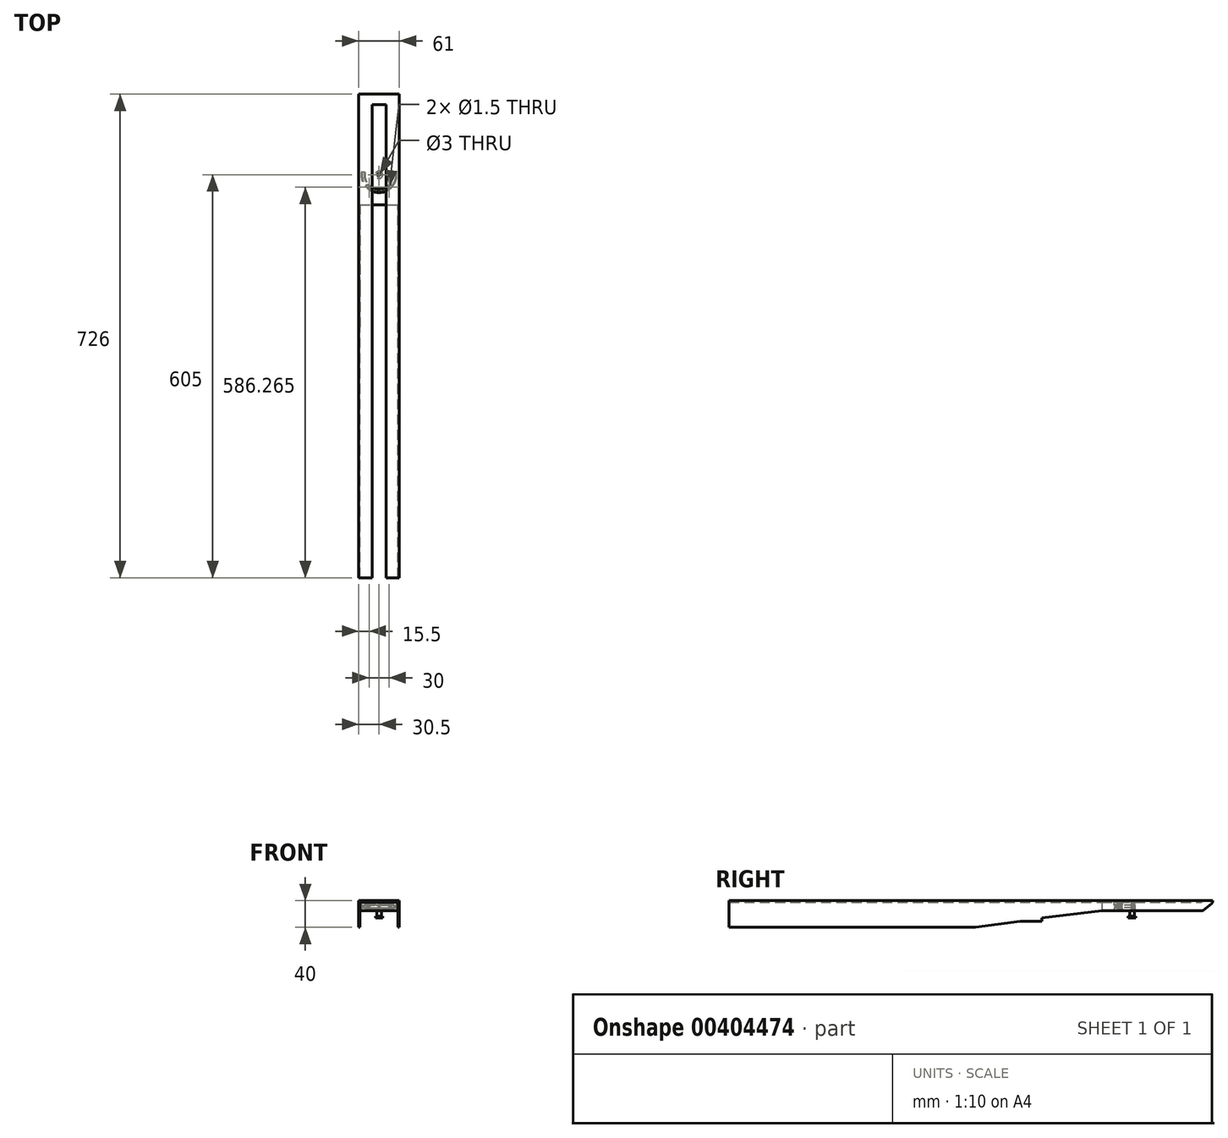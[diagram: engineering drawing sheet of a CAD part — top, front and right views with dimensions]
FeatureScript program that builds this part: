
annotation { "Feature Type Name" : "Feature", "Feature Type Description" : "" }
export const myFeature = defineFeature(function(context is Context, id is Id, definition is map)
    precondition{}
    {
        {
            var Q0;
            Q0=qCreatedBy(makeId("Top.planeOp"),FACE);
            var sketch = newSketch(context, id + "F0", { "sketchPlane" : qUnion([Q0])});
            skCircle(sketch, "E0", {"center": v(0, 0) * mm, "radius": 3.5 * mm});
            skLineSegment(sketch, "E1", {"start": v(-3.5, 0) * mm, "end": v(-3.5, -15.5) * mm});
            skLineSegment(sketch, "E2", {"start": v(3.5, 0) * mm, "end": v(3.5, -15.5) * mm});
            skLineSegment(sketch, "E3", {"start": v(-3.5, -15.5) * mm, "end": v(-7.78, -32.07) * mm});
            skLineSegment(sketch, "E4", {"start": v(3.5, -15.5) * mm, "end": v(7.78, -32.07) * mm});
            skLineSegment(sketch, "E5", {"start": v(-3.5, -15.5) * mm, "end": v(3.5, -15.5) * mm, "construction": true});
            skCircle(sketch, "E6", {"center": v(0, 0) * mm, "radius": 33 * mm});
            skLineSegment(sketch, "E7", {"start": v(-7.78, -32.07) * mm, "end": v(7.78, -32.07) * mm});
            skSolve(sketch);
        }
        {
            var Q0;
            Q0=qCreatedBy(makeId("Top.planeOp"),FACE);
            var sketch = newSketch(context, id + "F1", { "sketchPlane" : qUnion([Q0])});
            skLineSegment(sketch, "E8.bottom", {"start": v(-28.5, 105) * mm, "end": v(28.5, 105) * mm});
            skLineSegment(sketch, "E8.top", {"start": v(-28.5, -45) * mm, "end": v(28.5, -45) * mm});
            skLineSegment(sketch, "E8.left", {"start": v(-28.5, 105) * mm, "end": v(-28.5, -45) * mm});
            skLineSegment(sketch, "E8.right", {"start": v(28.5, 105) * mm, "end": v(28.5, -45) * mm});
            skPoint(sketch, "E8.middle", {"position": v(0, 0) * mm});
            skLineSegment(sketch, "E9", {"start": v(0, 105) * mm, "end": v(0, -45) * mm, "construction": true});
            skSolve(sketch);
        }
        {
            var Q0;
            Q0 = qSketchRegion(id + "F1", true);
            extrude(context, id + "F2", {"entities" : qUnion([Q0]), "depth" : 13 * mm});
        }
        {
            var Q0;
            Q0=qCreatedBy(makeId("Top.planeOp"),FACE);
            var sketch = newSketch(context, id + "F3", { "sketchPlane" : qUnion([Q0])});
            skLineSegment(sketch, "E10.bottom", {"start": v(-28.5, 33) * mm, "end": v(28.5, 33) * mm});
            skLineSegment(sketch, "E10.top", {"start": v(-28.5, -33) * mm, "end": v(28.5, -33) * mm});
            skLineSegment(sketch, "E10.left", {"start": v(-28.5, 33) * mm, "end": v(-28.5, -33) * mm});
            skLineSegment(sketch, "E10.right", {"start": v(28.5, 33) * mm, "end": v(28.5, -33) * mm});
            skPoint(sketch, "E10.middle", {"position": v(0, 0) * mm});
            skLineSegment(sketch, "E11.2", {"start": v(3.37, -15) * mm, "end": v(8.02, -33) * mm});
            skLineSegment(sketch, "E11.3", {"start": v(-3.37, -15) * mm, "end": v(-8.02, -33) * mm});
            skPoint(sketch, "E12.orphan", {"position": v(-3.5, 0) * mm});
            skPoint(sketch, "E13.orphan", {"position": v(3.5, 0) * mm});
            skLineSegment(sketch, "E14", {"start": v(-3.37, -15) * mm, "end": v(3.37, -15) * mm});
            skPoint(sketch, "E15.orphan", {"position": v(3.5, -15.5) * mm});
            skPoint(sketch, "E16.orphan", {"position": v(-3.5, -15.5) * mm});
            skPoint(sketch, "E17.orphan", {"position": v(-7.78, -32.07) * mm});
            skPoint(sketch, "E18.orphan", {"position": v(7.78, -32.07) * mm});
            skCircle(sketch, "E19", {"center": v(0, 0) * mm, "radius": 24 * mm, "construction": true});
            skCircle(sketch, "E20", {"center": v(0, 0) * mm, "radius": 26.5 * mm});
            skLineSegment(sketch, "E21", {"start": v(0, 0) * mm, "end": v(26.01, -21.83) * mm});
            skLineSegment(sketch, "E22", {"start": v(0, 0) * mm, "end": v(-26.01, -21.83) * mm});
            skCircle(sketch, "E23", {"center": v(0, 0) * mm, "radius": 21.5 * mm});
            skCircle(sketch, "E24", {"center": v(0, 0) * mm, "radius": 5.5 * mm});
            skLineSegment(sketch, "E25", {"start": v(0, 0) * mm, "end": v(-38.48, 6.79) * mm});
            skLineSegment(sketch, "E26", {"start": v(0, 0) * mm, "end": v(34.56, 6.1) * mm});
            skCircle(sketch, "E27", {"center": v(0, 0) * mm, "radius": 33.96 * mm, "construction": true});
            skCircle(sketch, "E28", {"center": v(0, 0) * mm, "radius": 40.5 * mm});
            skCircle(sketch, "E29", {"center": v(-17.7, -36.42) * mm, "radius": 1.98 * mm});
            skCircle(sketch, "E30", {"center": v(0, 0) * mm, "radius": 25.25 * mm});
            skCircle(sketch, "E31", {"center": v(0, 0) * mm, "radius": 22.75 * mm});
            skCircle(sketch, "E32", {"center": v(0, 0) * mm, "radius": 26.75 * mm});
            skCircle(sketch, "E33", {"center": v(0, 0) * mm, "radius": 21.25 * mm});
            skCircle(sketch, "E34", {"center": v(0, 0) * mm, "radius": 22.5 * mm});
            skCircle(sketch, "E35", {"center": v(0, 0) * mm, "radius": 25.5 * mm});
            skPoint(sketch, "E36", {"position": v(-15, -18.73) * mm});
            skPoint(sketch, "E37", {"position": v(15, -18.73) * mm});
            skSolve(sketch);
        }
        {
            var Q0;
            {var subQ0=sQuery(id+"F3.wireOp",EDGE,"E30");var subQ1=sQuery(id+"F3.wireOp",EDGE,"E11.2");var subQ2=makeQuery(id+"F3.imprint","INTERSECT",VERTEX,{"derivedFrom":[subQ1,subQ0]});Q0=makeQuery(id+"F3.imprint","IMPRINT",FACE,{"disambiguationData":[TD([[makeQuery(id+"F3.imprint","IMPRINT",EDGE,{"disambiguationData":[TD([[subQ2,-1.0]])],"derivedFrom":subQ1}),-1.0]])]});}
            var Q1;
            {var subQ0=sQuery(id+"F3.wireOp",EDGE,"E30");var subQ1=sQuery(id+"F3.wireOp",EDGE,"E11.3");var subQ2=makeQuery(id+"F3.imprint","INTERSECT",VERTEX,{"derivedFrom":[subQ1,subQ0]});Q1=makeQuery(id+"F3.imprint","IMPRINT",FACE,{"disambiguationData":[TD([[makeQuery(id+"F3.imprint","IMPRINT",EDGE,{"disambiguationData":[TD([[subQ2,-1.0]])],"derivedFrom":subQ1}),-1.0]])]});}
            var Q2;
            {var subQ0=sQuery(id+"F3.wireOp",EDGE,"E23");var subQ1=sQuery(id+"F3.wireOp",EDGE,"E11.3");var subQ2=makeQuery(id+"F3.imprint","INTERSECT",VERTEX,{"derivedFrom":[subQ1,subQ0]});Q2=makeQuery(id+"F3.imprint","IMPRINT",FACE,{"disambiguationData":[TD([[makeQuery(id+"F3.imprint","IMPRINT",EDGE,{"disambiguationData":[TD([[subQ2,-1.0]])],"derivedFrom":subQ1}),-1.0]])]});}
            var Q3;
            {var subQ0=sQuery(id+"F3.wireOp",EDGE,"E31");var subQ1=sQuery(id+"F3.wireOp",EDGE,"E11.3");var subQ2=makeQuery(id+"F3.imprint","INTERSECT",VERTEX,{"derivedFrom":[subQ1,subQ0]});Q3=makeQuery(id+"F3.imprint","IMPRINT",FACE,{"disambiguationData":[TD([[makeQuery(id+"F3.imprint","IMPRINT",EDGE,{"disambiguationData":[TD([[subQ2,-1.0]])],"derivedFrom":subQ1}),-1.0]])]});}
            var Q4;
            {var subQ0=sQuery(id+"F3.wireOp",EDGE,"E31");var subQ1=sQuery(id+"F3.wireOp",EDGE,"E11.2");var subQ2=makeQuery(id+"F3.imprint","INTERSECT",VERTEX,{"derivedFrom":[subQ1,subQ0]});Q4=makeQuery(id+"F3.imprint","IMPRINT",FACE,{"disambiguationData":[TD([[makeQuery(id+"F3.imprint","IMPRINT",EDGE,{"disambiguationData":[TD([[subQ2,-1.0]])],"derivedFrom":subQ1}),-1.0]])]});}
            var Q5;
            {var subQ0=sQuery(id+"F3.wireOp",EDGE,"E30");var subQ1=sQuery(id+"F3.wireOp",EDGE,"E11.2");var subQ2=makeQuery(id+"F3.imprint","INTERSECT",VERTEX,{"derivedFrom":[subQ1,subQ0]});Q5=makeQuery(id+"F3.imprint","IMPRINT",FACE,{"disambiguationData":[TD([[makeQuery(id+"F3.imprint","IMPRINT",EDGE,{"disambiguationData":[TD([[subQ2,-1.0]])],"derivedFrom":subQ1}),1.0]])]});}
            var Q6;
            {var subQ0=sQuery(id+"F3.wireOp",EDGE,"E31");var subQ1=sQuery(id+"F3.wireOp",EDGE,"E11.2");var subQ2=makeQuery(id+"F3.imprint","INTERSECT",VERTEX,{"derivedFrom":[subQ1,subQ0]});Q6=makeQuery(id+"F3.imprint","IMPRINT",FACE,{"disambiguationData":[TD([[makeQuery(id+"F3.imprint","IMPRINT",EDGE,{"disambiguationData":[TD([[subQ2,-1.0]])],"derivedFrom":subQ1}),1.0]])]});}
            var Q7;
            {var subQ0=sQuery(id+"F3.wireOp",EDGE,"E23");var subQ1=sQuery(id+"F3.wireOp",EDGE,"E11.2");var subQ2=makeQuery(id+"F3.imprint","INTERSECT",VERTEX,{"derivedFrom":[subQ1,subQ0]});Q7=makeQuery(id+"F3.imprint","IMPRINT",FACE,{"disambiguationData":[TD([[makeQuery(id+"F3.imprint","IMPRINT",EDGE,{"disambiguationData":[TD([[subQ2,-1.0]])],"derivedFrom":subQ1}),1.0]])]});}
            var Q8;
            {var subQ0=sQuery(id+"F3.wireOp",EDGE,"E23");var subQ1=sQuery(id+"F3.wireOp",EDGE,"E11.2");var subQ2=makeQuery(id+"F3.imprint","INTERSECT",VERTEX,{"derivedFrom":[subQ1,subQ0]});Q8=makeQuery(id+"F3.imprint","IMPRINT",FACE,{"disambiguationData":[TD([[makeQuery(id+"F3.imprint","IMPRINT",EDGE,{"disambiguationData":[TD([[subQ2,-1.0]])],"derivedFrom":subQ1}),-1.0]])]});}
            var Q9;
            {var subQ0=sQuery(id+"F3.wireOp",EDGE,"E23");var subQ1=sQuery(id+"F3.wireOp",EDGE,"E21");var subQ2=makeQuery(id+"F3.imprint","INTERSECT",VERTEX,{"derivedFrom":[subQ1,subQ0]});Q9=makeQuery(id+"F3.imprint","IMPRINT",FACE,{"disambiguationData":[TD([[makeQuery(id+"F3.imprint","IMPRINT",EDGE,{"disambiguationData":[TD([[subQ2,-1.0]])],"derivedFrom":subQ1}),1.0]])]});}
            var Q10;
            {var subQ0=sQuery(id+"F3.wireOp",EDGE,"E31");var subQ1=sQuery(id+"F3.wireOp",EDGE,"E21");var subQ2=makeQuery(id+"F3.imprint","INTERSECT",VERTEX,{"derivedFrom":[subQ1,subQ0]});Q10=makeQuery(id+"F3.imprint","IMPRINT",FACE,{"disambiguationData":[TD([[makeQuery(id+"F3.imprint","IMPRINT",EDGE,{"disambiguationData":[TD([[subQ2,-1.0]])],"derivedFrom":subQ1}),1.0]])]});}
            var Q11;
            {var subQ0=sQuery(id+"F3.wireOp",EDGE,"E21");var subQ1=sQuery(id+"F3.wireOp",EDGE,"E20");var subQ2=makeQuery(id+"F3.imprint","INTERSECT",VERTEX,{"derivedFrom":[subQ1,subQ0]});Q11=makeQuery(id+"F3.imprint","IMPRINT",FACE,{"disambiguationData":[TD([[makeQuery(id+"F3.imprint","IMPRINT",EDGE,{"disambiguationData":[TD([[subQ2,-1.0]])],"derivedFrom":subQ1}),1.0]])]});}
            var Q12;
            {var subQ0=sQuery(id+"F3.wireOp",EDGE,"E22");var subQ1=sQuery(id+"F3.wireOp",EDGE,"E20");var subQ2=makeQuery(id+"F3.imprint","INTERSECT",VERTEX,{"derivedFrom":[subQ1,subQ0]});Q12=makeQuery(id+"F3.imprint","IMPRINT",FACE,{"disambiguationData":[TD([[makeQuery(id+"F3.imprint","IMPRINT",EDGE,{"disambiguationData":[TD([[subQ2,1.0]])],"derivedFrom":subQ1}),1.0]])]});}
            var Q13;
            {var subQ0=sQuery(id+"F3.wireOp",EDGE,"E31");var subQ1=sQuery(id+"F3.wireOp",EDGE,"E22");var subQ2=makeQuery(id+"F3.imprint","INTERSECT",VERTEX,{"derivedFrom":[subQ1,subQ0]});Q13=makeQuery(id+"F3.imprint","IMPRINT",FACE,{"disambiguationData":[TD([[makeQuery(id+"F3.imprint","IMPRINT",EDGE,{"disambiguationData":[TD([[subQ2,-1.0]])],"derivedFrom":subQ1}),-1.0]])]});}
            var Q14;
            {var subQ0=sQuery(id+"F3.wireOp",EDGE,"E23");var subQ1=sQuery(id+"F3.wireOp",EDGE,"E22");var subQ2=makeQuery(id+"F3.imprint","INTERSECT",VERTEX,{"derivedFrom":[subQ1,subQ0]});Q14=makeQuery(id+"F3.imprint","IMPRINT",FACE,{"disambiguationData":[TD([[makeQuery(id+"F3.imprint","IMPRINT",EDGE,{"disambiguationData":[TD([[subQ2,-1.0]])],"derivedFrom":subQ1}),-1.0]])]});}
            var Q15;
            {var subQ0=sQuery(id+"F3.wireOp",EDGE,"E20");var subQ1=sQuery(id+"F3.wireOp",EDGE,"E11.2");var subQ2=makeQuery(id+"F3.imprint","INTERSECT",VERTEX,{"derivedFrom":[subQ1,subQ0]});Q15=makeQuery(id+"F3.imprint","IMPRINT",FACE,{"disambiguationData":[TD([[makeQuery(id+"F3.imprint","IMPRINT",EDGE,{"disambiguationData":[TD([[subQ2,-1.0]])],"derivedFrom":subQ1}),-1.0]])]});}
            var Q16;
            {var subQ0=sQuery(id+"F3.wireOp",EDGE,"E20");var subQ1=sQuery(id+"F3.wireOp",EDGE,"E11.3");var subQ2=makeQuery(id+"F3.imprint","INTERSECT",VERTEX,{"derivedFrom":[subQ1,subQ0]});Q16=makeQuery(id+"F3.imprint","IMPRINT",FACE,{"disambiguationData":[TD([[makeQuery(id+"F3.imprint","IMPRINT",EDGE,{"disambiguationData":[TD([[subQ2,-1.0]])],"derivedFrom":subQ1}),-1.0]])]});}
            var Q17;
            {var subQ0=sQuery(id+"F3.wireOp",EDGE,"E20");var subQ1=sQuery(id+"F3.wireOp",EDGE,"E11.2");var subQ2=makeQuery(id+"F3.imprint","INTERSECT",VERTEX,{"derivedFrom":[subQ1,subQ0]});Q17=makeQuery(id+"F3.imprint","IMPRINT",FACE,{"disambiguationData":[TD([[makeQuery(id+"F3.imprint","IMPRINT",EDGE,{"disambiguationData":[TD([[subQ2,-1.0]])],"derivedFrom":subQ1}),1.0]])]});}
            var Q18;
            {var subQ0=sQuery(id+"F3.wireOp",EDGE,"E33");var subQ1=sQuery(id+"F3.wireOp",EDGE,"E11.2");var subQ2=makeQuery(id+"F3.imprint","INTERSECT",VERTEX,{"derivedFrom":[subQ1,subQ0]});Q18=makeQuery(id+"F3.imprint","IMPRINT",FACE,{"disambiguationData":[TD([[makeQuery(id+"F3.imprint","IMPRINT",EDGE,{"disambiguationData":[TD([[subQ2,-1.0]])],"derivedFrom":subQ1}),1.0]])]});}
            var Q19;
            {var subQ0=sQuery(id+"F3.wireOp",EDGE,"E33");var subQ1=sQuery(id+"F3.wireOp",EDGE,"E11.2");var subQ2=makeQuery(id+"F3.imprint","INTERSECT",VERTEX,{"derivedFrom":[subQ1,subQ0]});Q19=makeQuery(id+"F3.imprint","IMPRINT",FACE,{"disambiguationData":[TD([[makeQuery(id+"F3.imprint","IMPRINT",EDGE,{"disambiguationData":[TD([[subQ2,-1.0]])],"derivedFrom":subQ1}),-1.0]])]});}
            var Q20;
            {var subQ0=sQuery(id+"F3.wireOp",EDGE,"E33");var subQ1=sQuery(id+"F3.wireOp",EDGE,"E11.3");var subQ2=makeQuery(id+"F3.imprint","INTERSECT",VERTEX,{"derivedFrom":[subQ1,subQ0]});Q20=makeQuery(id+"F3.imprint","IMPRINT",FACE,{"disambiguationData":[TD([[makeQuery(id+"F3.imprint","IMPRINT",EDGE,{"disambiguationData":[TD([[subQ2,-1.0]])],"derivedFrom":subQ1}),-1.0]])]});}
            var Q21;
            {var subQ0=sQuery(id+"F3.wireOp",EDGE,"E33");var subQ1=sQuery(id+"F3.wireOp",EDGE,"E22");var subQ2=makeQuery(id+"F3.imprint","INTERSECT",VERTEX,{"derivedFrom":[subQ1,subQ0]});Q21=makeQuery(id+"F3.imprint","IMPRINT",FACE,{"disambiguationData":[TD([[makeQuery(id+"F3.imprint","IMPRINT",EDGE,{"disambiguationData":[TD([[subQ2,-1.0]])],"derivedFrom":subQ1}),-1.0]])]});}
            var Q22;
            {var subQ0=sQuery(id+"F3.wireOp",EDGE,"E25");var subQ1=sQuery(id+"F3.wireOp",EDGE,"E20");var subQ2=makeQuery(id+"F3.imprint","INTERSECT",VERTEX,{"derivedFrom":[subQ1,subQ0]});Q22=makeQuery(id+"F3.imprint","IMPRINT",FACE,{"disambiguationData":[TD([[makeQuery(id+"F3.imprint","IMPRINT",EDGE,{"disambiguationData":[TD([[subQ2,-1.0]])],"derivedFrom":subQ1}),-1.0]])]});}
            var Q23;
            {var subQ0=sQuery(id+"F3.wireOp",EDGE,"E26");var subQ1=sQuery(id+"F3.wireOp",EDGE,"E20");var subQ2=makeQuery(id+"F3.imprint","INTERSECT",VERTEX,{"derivedFrom":[subQ1,subQ0]});Q23=makeQuery(id+"F3.imprint","IMPRINT",FACE,{"disambiguationData":[TD([[makeQuery(id+"F3.imprint","IMPRINT",EDGE,{"disambiguationData":[TD([[subQ2,1.0]])],"derivedFrom":subQ1}),-1.0]])]});}
            var Q24;
            {var subQ0=sQuery(id+"F3.wireOp",EDGE,"E33");var subQ1=sQuery(id+"F3.wireOp",EDGE,"E21");var subQ2=makeQuery(id+"F3.imprint","INTERSECT",VERTEX,{"derivedFrom":[subQ1,subQ0]});Q24=makeQuery(id+"F3.imprint","IMPRINT",FACE,{"disambiguationData":[TD([[makeQuery(id+"F3.imprint","IMPRINT",EDGE,{"disambiguationData":[TD([[subQ2,-1.0]])],"derivedFrom":subQ1}),1.0]])]});}
            var Q25;
            {var subQ0=sQuery(id+"F3.wireOp",EDGE,"E30");var subQ1=sQuery(id+"F3.wireOp",EDGE,"E22");var subQ2=makeQuery(id+"F3.imprint","INTERSECT",VERTEX,{"derivedFrom":[subQ1,subQ0]});Q25=makeQuery(id+"F3.imprint","IMPRINT",FACE,{"disambiguationData":[TD([[makeQuery(id+"F3.imprint","IMPRINT",EDGE,{"disambiguationData":[TD([[subQ2,-1.0]])],"derivedFrom":subQ1}),-1.0]])]});}
            var Q26;
            {var subQ0=sQuery(id+"F3.wireOp",EDGE,"E35");var subQ1=sQuery(id+"F3.wireOp",EDGE,"E11.3");var subQ2=makeQuery(id+"F3.imprint","INTERSECT",VERTEX,{"derivedFrom":[subQ1,subQ0]});Q26=makeQuery(id+"F3.imprint","IMPRINT",FACE,{"disambiguationData":[TD([[makeQuery(id+"F3.imprint","IMPRINT",EDGE,{"disambiguationData":[TD([[subQ2,-1.0]])],"derivedFrom":subQ1}),-1.0]])]});}
            var Q27;
            {var subQ0=sQuery(id+"F3.wireOp",EDGE,"E34");var subQ1=sQuery(id+"F3.wireOp",EDGE,"E11.3");var subQ2=makeQuery(id+"F3.imprint","INTERSECT",VERTEX,{"derivedFrom":[subQ1,subQ0]});Q27=makeQuery(id+"F3.imprint","IMPRINT",FACE,{"disambiguationData":[TD([[makeQuery(id+"F3.imprint","IMPRINT",EDGE,{"disambiguationData":[TD([[subQ2,-1.0]])],"derivedFrom":subQ1}),-1.0]])]});}
            var Q28;
            {var subQ0=sQuery(id+"F3.wireOp",EDGE,"E34");var subQ1=sQuery(id+"F3.wireOp",EDGE,"E22");var subQ2=makeQuery(id+"F3.imprint","INTERSECT",VERTEX,{"derivedFrom":[subQ1,subQ0]});Q28=makeQuery(id+"F3.imprint","IMPRINT",FACE,{"disambiguationData":[TD([[makeQuery(id+"F3.imprint","IMPRINT",EDGE,{"disambiguationData":[TD([[subQ2,-1.0]])],"derivedFrom":subQ1}),-1.0]])]});}
            var Q29;
            {var subQ0=sQuery(id+"F3.wireOp",EDGE,"E35");var subQ1=sQuery(id+"F3.wireOp",EDGE,"E11.2");var subQ2=makeQuery(id+"F3.imprint","INTERSECT",VERTEX,{"derivedFrom":[subQ1,subQ0]});Q29=makeQuery(id+"F3.imprint","IMPRINT",FACE,{"disambiguationData":[TD([[makeQuery(id+"F3.imprint","IMPRINT",EDGE,{"disambiguationData":[TD([[subQ2,-1.0]])],"derivedFrom":subQ1}),1.0]])]});}
            var Q30;
            {var subQ0=sQuery(id+"F3.wireOp",EDGE,"E34");var subQ1=sQuery(id+"F3.wireOp",EDGE,"E11.2");var subQ2=makeQuery(id+"F3.imprint","INTERSECT",VERTEX,{"derivedFrom":[subQ1,subQ0]});Q30=makeQuery(id+"F3.imprint","IMPRINT",FACE,{"disambiguationData":[TD([[makeQuery(id+"F3.imprint","IMPRINT",EDGE,{"disambiguationData":[TD([[subQ2,-1.0]])],"derivedFrom":subQ1}),1.0]])]});}
            var Q31;
            {var subQ0=sQuery(id+"F3.wireOp",EDGE,"E35");var subQ1=sQuery(id+"F3.wireOp",EDGE,"E11.2");var subQ2=makeQuery(id+"F3.imprint","INTERSECT",VERTEX,{"derivedFrom":[subQ1,subQ0]});Q31=makeQuery(id+"F3.imprint","IMPRINT",FACE,{"disambiguationData":[TD([[makeQuery(id+"F3.imprint","IMPRINT",EDGE,{"disambiguationData":[TD([[subQ2,-1.0]])],"derivedFrom":subQ1}),-1.0]])]});}
            var Q32;
            {var subQ0=sQuery(id+"F3.wireOp",EDGE,"E34");var subQ1=sQuery(id+"F3.wireOp",EDGE,"E11.2");var subQ2=makeQuery(id+"F3.imprint","INTERSECT",VERTEX,{"derivedFrom":[subQ1,subQ0]});Q32=makeQuery(id+"F3.imprint","IMPRINT",FACE,{"disambiguationData":[TD([[makeQuery(id+"F3.imprint","IMPRINT",EDGE,{"disambiguationData":[TD([[subQ2,-1.0]])],"derivedFrom":subQ1}),-1.0]])]});}
            var Q33;
            {var subQ0=sQuery(id+"F3.wireOp",EDGE,"E34");var subQ1=sQuery(id+"F3.wireOp",EDGE,"E21");var subQ2=makeQuery(id+"F3.imprint","INTERSECT",VERTEX,{"derivedFrom":[subQ1,subQ0]});Q33=makeQuery(id+"F3.imprint","IMPRINT",FACE,{"disambiguationData":[TD([[makeQuery(id+"F3.imprint","IMPRINT",EDGE,{"disambiguationData":[TD([[subQ2,-1.0]])],"derivedFrom":subQ1}),1.0]])]});}
            var Q34;
            {var subQ0=sQuery(id+"F3.wireOp",EDGE,"E30");var subQ1=sQuery(id+"F3.wireOp",EDGE,"E21");var subQ2=makeQuery(id+"F3.imprint","INTERSECT",VERTEX,{"derivedFrom":[subQ1,subQ0]});Q34=makeQuery(id+"F3.imprint","IMPRINT",FACE,{"disambiguationData":[TD([[makeQuery(id+"F3.imprint","IMPRINT",EDGE,{"disambiguationData":[TD([[subQ2,-1.0]])],"derivedFrom":subQ1}),1.0]])]});}
            extrude(context, id + "F4", {"entities" : qUnion([Q0, Q1, Q2, Q3, Q4, Q5, Q6, Q7, Q8, Q9, Q10, Q11, Q12, Q13, Q14, Q15, Q16, Q17, Q18, Q19, Q20, Q21, Q22, Q23, Q24, Q25, Q26, Q27, Q28, Q29, Q30, Q31, Q32, Q33, Q34]), "operationType" : NewBodyOperationType.REMOVE, "depth" : 4.5 * mm});
        }
        {
            var Q0;
            Q0=sQuery(id+"F0.wireOp",VERTEX,"E6.center");
            var Q1;
            Q1=makeQuery(id+"F2.opExtrude","SWEPT_BODY",BODY,{"disambiguationData":[OSD([sQuery(id+"F1.wireOp",EDGE,"E8.bottom"),sQuery(id+"F1.wireOp",EDGE,"E8.top"),sQuery(id+"F1.wireOp",EDGE,"E8.left"),sQuery(id+"F1.wireOp",EDGE,"E8.right")])]});
            hole(context, id + "F5", {"style" : HoleStyle.SIMPLE, "endStyle" : HoleEndStyle.THROUGH, "oppositeDirection" : true, "holeDiameter" : 3 * mm, "tappedDepth" : 12 * mm, "tapClearance" : 3, "locations" : qUnion([Q0]), "scope" : qUnion([Q1])});
        }
        {
            var Q0;
            Q0=makeQuery(id+"F2.opExtrude","CAP_FACE",FACE,{"disambiguationData":[OSD([sQuery(id+"F1.wireOp",EDGE,"E8.bottom"),sQuery(id+"F1.wireOp",EDGE,"E8.top"),sQuery(id+"F1.wireOp",EDGE,"E8.left"),sQuery(id+"F1.wireOp",EDGE,"E8.right")])],"isStart":false});
            var sketch = newSketch(context, id + "F6", { "sketchPlane" : qUnion([Q0])});
            skArc(sketch, "E38", {"start": v(20.93, 3.7) * mm, "mid": v(0, -21.25) * mm, "end": v(-20.93, 3.7) * mm});
            skArc(sketch, "E39", {"start": v(-26.34, 4.65) * mm, "mid": v(0, -26.75) * mm, "end": v(26.34, 4.65) * mm});
            skLineSegment(sketch, "E40", {"start": v(20.93, 3.7) * mm, "end": v(26.34, 4.65) * mm});
            skLineSegment(sketch, "E41", {"start": v(-26.34, 4.65) * mm, "end": v(-20.93, 3.7) * mm});
            skSolve(sketch);
        }
        {
            var Q0;
            Q0 = qSketchRegion(id + "F6", true);
            extrude(context, id + "F7", {"entities" : qUnion([Q0]), "operationType" : NewBodyOperationType.REMOVE, "oppositeDirection" : true, "depth" : 4.5 * mm});
        }
        {
            var Q0;
            {var subQ0=sQuery(id+"F3.wireOp",EDGE,"E31");var subQ1=sQuery(id+"F3.wireOp",EDGE,"E11.2");var subQ2=makeQuery(id+"F3.imprint","INTERSECT",VERTEX,{"derivedFrom":[subQ1,subQ0]});Q0=makeQuery(id+"F3.imprint","IMPRINT",FACE,{"disambiguationData":[TD([[makeQuery(id+"F3.imprint","IMPRINT",EDGE,{"disambiguationData":[TD([[subQ2,-1.0]])],"derivedFrom":subQ1}),-1.0]])]});}
            var Q1;
            {var subQ0=sQuery(id+"F3.wireOp",EDGE,"E30");var subQ1=sQuery(id+"F3.wireOp",EDGE,"E11.2");var subQ2=makeQuery(id+"F3.imprint","INTERSECT",VERTEX,{"derivedFrom":[subQ1,subQ0]});Q1=makeQuery(id+"F3.imprint","IMPRINT",FACE,{"disambiguationData":[TD([[makeQuery(id+"F3.imprint","IMPRINT",EDGE,{"disambiguationData":[TD([[subQ2,-1.0]])],"derivedFrom":subQ1}),-1.0]])]});}
            var Q2;
            {var subQ0=sQuery(id+"F3.wireOp",EDGE,"E34");var subQ1=sQuery(id+"F3.wireOp",EDGE,"E11.2");var subQ2=makeQuery(id+"F3.imprint","INTERSECT",VERTEX,{"derivedFrom":[subQ1,subQ0]});Q2=makeQuery(id+"F3.imprint","IMPRINT",FACE,{"disambiguationData":[TD([[makeQuery(id+"F3.imprint","IMPRINT",EDGE,{"disambiguationData":[TD([[subQ2,-1.0]])],"derivedFrom":subQ1}),-1.0]])]});}
            var Q3;
            {var subQ0=sQuery(id+"F3.wireOp",EDGE,"E34");var subQ1=sQuery(id+"F3.wireOp",EDGE,"E11.3");var subQ2=makeQuery(id+"F3.imprint","INTERSECT",VERTEX,{"derivedFrom":[subQ1,subQ0]});Q3=makeQuery(id+"F3.imprint","IMPRINT",FACE,{"disambiguationData":[TD([[makeQuery(id+"F3.imprint","IMPRINT",EDGE,{"disambiguationData":[TD([[subQ2,-1.0]])],"derivedFrom":subQ1}),-1.0]])]});}
            var Q4;
            {var subQ0=sQuery(id+"F3.wireOp",EDGE,"E31");var subQ1=sQuery(id+"F3.wireOp",EDGE,"E11.3");var subQ2=makeQuery(id+"F3.imprint","INTERSECT",VERTEX,{"derivedFrom":[subQ1,subQ0]});Q4=makeQuery(id+"F3.imprint","IMPRINT",FACE,{"disambiguationData":[TD([[makeQuery(id+"F3.imprint","IMPRINT",EDGE,{"disambiguationData":[TD([[subQ2,-1.0]])],"derivedFrom":subQ1}),-1.0]])]});}
            var Q5;
            {var subQ0=sQuery(id+"F3.wireOp",EDGE,"E30");var subQ1=sQuery(id+"F3.wireOp",EDGE,"E11.3");var subQ2=makeQuery(id+"F3.imprint","INTERSECT",VERTEX,{"derivedFrom":[subQ1,subQ0]});Q5=makeQuery(id+"F3.imprint","IMPRINT",FACE,{"disambiguationData":[TD([[makeQuery(id+"F3.imprint","IMPRINT",EDGE,{"disambiguationData":[TD([[subQ2,-1.0]])],"derivedFrom":subQ1}),-1.0]])]});}
            var Q6;
            {var subQ0=sQuery(id+"F3.wireOp",EDGE,"E30");var subQ1=sQuery(id+"F3.wireOp",EDGE,"E22");var subQ2=makeQuery(id+"F3.imprint","INTERSECT",VERTEX,{"derivedFrom":[subQ1,subQ0]});Q6=makeQuery(id+"F3.imprint","IMPRINT",FACE,{"disambiguationData":[TD([[makeQuery(id+"F3.imprint","IMPRINT",EDGE,{"disambiguationData":[TD([[subQ2,-1.0]])],"derivedFrom":subQ1}),-1.0]])]});}
            var Q7;
            {var subQ0=sQuery(id+"F3.wireOp",EDGE,"E31");var subQ1=sQuery(id+"F3.wireOp",EDGE,"E22");var subQ2=makeQuery(id+"F3.imprint","INTERSECT",VERTEX,{"derivedFrom":[subQ1,subQ0]});Q7=makeQuery(id+"F3.imprint","IMPRINT",FACE,{"disambiguationData":[TD([[makeQuery(id+"F3.imprint","IMPRINT",EDGE,{"disambiguationData":[TD([[subQ2,-1.0]])],"derivedFrom":subQ1}),-1.0]])]});}
            var Q8;
            {var subQ0=sQuery(id+"F3.wireOp",EDGE,"E34");var subQ1=sQuery(id+"F3.wireOp",EDGE,"E22");var subQ2=makeQuery(id+"F3.imprint","INTERSECT",VERTEX,{"derivedFrom":[subQ1,subQ0]});Q8=makeQuery(id+"F3.imprint","IMPRINT",FACE,{"disambiguationData":[TD([[makeQuery(id+"F3.imprint","IMPRINT",EDGE,{"disambiguationData":[TD([[subQ2,-1.0]])],"derivedFrom":subQ1}),-1.0]])]});}
            var Q9;
            {var subQ0=sQuery(id+"F3.wireOp",EDGE,"E31");var subQ1=sQuery(id+"F3.wireOp",EDGE,"E11.2");var subQ2=makeQuery(id+"F3.imprint","INTERSECT",VERTEX,{"derivedFrom":[subQ1,subQ0]});Q9=makeQuery(id+"F3.imprint","IMPRINT",FACE,{"disambiguationData":[TD([[makeQuery(id+"F3.imprint","IMPRINT",EDGE,{"disambiguationData":[TD([[subQ2,-1.0]])],"derivedFrom":subQ1}),1.0]])]});}
            var Q10;
            {var subQ0=sQuery(id+"F3.wireOp",EDGE,"E31");var subQ1=sQuery(id+"F3.wireOp",EDGE,"E21");var subQ2=makeQuery(id+"F3.imprint","INTERSECT",VERTEX,{"derivedFrom":[subQ1,subQ0]});Q10=makeQuery(id+"F3.imprint","IMPRINT",FACE,{"disambiguationData":[TD([[makeQuery(id+"F3.imprint","IMPRINT",EDGE,{"disambiguationData":[TD([[subQ2,-1.0]])],"derivedFrom":subQ1}),1.0]])]});}
            var Q11;
            {var subQ0=sQuery(id+"F3.wireOp",EDGE,"E34");var subQ1=sQuery(id+"F3.wireOp",EDGE,"E21");var subQ2=makeQuery(id+"F3.imprint","INTERSECT",VERTEX,{"derivedFrom":[subQ1,subQ0]});Q11=makeQuery(id+"F3.imprint","IMPRINT",FACE,{"disambiguationData":[TD([[makeQuery(id+"F3.imprint","IMPRINT",EDGE,{"disambiguationData":[TD([[subQ2,-1.0]])],"derivedFrom":subQ1}),1.0]])]});}
            var Q12;
            {var subQ0=sQuery(id+"F3.wireOp",EDGE,"E34");var subQ1=sQuery(id+"F3.wireOp",EDGE,"E11.2");var subQ2=makeQuery(id+"F3.imprint","INTERSECT",VERTEX,{"derivedFrom":[subQ1,subQ0]});Q12=makeQuery(id+"F3.imprint","IMPRINT",FACE,{"disambiguationData":[TD([[makeQuery(id+"F3.imprint","IMPRINT",EDGE,{"disambiguationData":[TD([[subQ2,-1.0]])],"derivedFrom":subQ1}),1.0]])]});}
            var Q13;
            {var subQ0=sQuery(id+"F3.wireOp",EDGE,"E30");var subQ1=sQuery(id+"F3.wireOp",EDGE,"E11.2");var subQ2=makeQuery(id+"F3.imprint","INTERSECT",VERTEX,{"derivedFrom":[subQ1,subQ0]});Q13=makeQuery(id+"F3.imprint","IMPRINT",FACE,{"disambiguationData":[TD([[makeQuery(id+"F3.imprint","IMPRINT",EDGE,{"disambiguationData":[TD([[subQ2,-1.0]])],"derivedFrom":subQ1}),1.0]])]});}
            var Q14;
            {var subQ0=sQuery(id+"F3.wireOp",EDGE,"E30");var subQ1=sQuery(id+"F3.wireOp",EDGE,"E21");var subQ2=makeQuery(id+"F3.imprint","INTERSECT",VERTEX,{"derivedFrom":[subQ1,subQ0]});Q14=makeQuery(id+"F3.imprint","IMPRINT",FACE,{"disambiguationData":[TD([[makeQuery(id+"F3.imprint","IMPRINT",EDGE,{"disambiguationData":[TD([[subQ2,-1.0]])],"derivedFrom":subQ1}),1.0]])]});}
            extrude(context, id + "F8", {"entities" : qUnion([Q0, Q1, Q2, Q3, Q4, Q5, Q6, Q7, Q8, Q9, Q10, Q11, Q12, Q13, Q14]), "operationType" : NewBodyOperationType.REMOVE, "depth" : 25 * mm});
        }
        {
            var Q0;
            {var subQ0=sQuery(id+"F3.wireOp",EDGE,"E23");var subQ1=sQuery(id+"F3.wireOp",EDGE,"E11.2");var subQ2=makeQuery(id+"F3.imprint","INTERSECT",VERTEX,{"derivedFrom":[subQ1,subQ0]});Q0=makeQuery(id+"F3.imprint","IMPRINT",FACE,{"disambiguationData":[TD([[makeQuery(id+"F3.imprint","IMPRINT",EDGE,{"disambiguationData":[TD([[subQ2,-1.0]])],"derivedFrom":subQ1}),1.0]])]});}
            var Q1;
            {var subQ0=sQuery(id+"F3.wireOp",EDGE,"E23");var subQ1=sQuery(id+"F3.wireOp",EDGE,"E11.2");var subQ2=makeQuery(id+"F3.imprint","INTERSECT",VERTEX,{"derivedFrom":[subQ1,subQ0]});Q1=makeQuery(id+"F3.imprint","IMPRINT",FACE,{"disambiguationData":[TD([[makeQuery(id+"F3.imprint","IMPRINT",EDGE,{"disambiguationData":[TD([[subQ2,-1.0]])],"derivedFrom":subQ1}),-1.0]])]});}
            var Q2;
            {var subQ0=sQuery(id+"F3.wireOp",EDGE,"E23");var subQ1=sQuery(id+"F3.wireOp",EDGE,"E11.3");var subQ2=makeQuery(id+"F3.imprint","INTERSECT",VERTEX,{"derivedFrom":[subQ1,subQ0]});Q2=makeQuery(id+"F3.imprint","IMPRINT",FACE,{"disambiguationData":[TD([[makeQuery(id+"F3.imprint","IMPRINT",EDGE,{"disambiguationData":[TD([[subQ2,-1.0]])],"derivedFrom":subQ1}),-1.0]])]});}
            var Q3;
            {var subQ0=sQuery(id+"F3.wireOp",EDGE,"E31");var subQ1=sQuery(id+"F3.wireOp",EDGE,"E11.3");var subQ2=makeQuery(id+"F3.imprint","INTERSECT",VERTEX,{"derivedFrom":[subQ1,subQ0]});Q3=makeQuery(id+"F3.imprint","IMPRINT",FACE,{"disambiguationData":[TD([[makeQuery(id+"F3.imprint","IMPRINT",EDGE,{"disambiguationData":[TD([[subQ2,-1.0]])],"derivedFrom":subQ1}),-1.0]])]});}
            var Q4;
            {var subQ0=sQuery(id+"F3.wireOp",EDGE,"E30");var subQ1=sQuery(id+"F3.wireOp",EDGE,"E11.3");var subQ2=makeQuery(id+"F3.imprint","INTERSECT",VERTEX,{"derivedFrom":[subQ1,subQ0]});Q4=makeQuery(id+"F3.imprint","IMPRINT",FACE,{"disambiguationData":[TD([[makeQuery(id+"F3.imprint","IMPRINT",EDGE,{"disambiguationData":[TD([[subQ2,-1.0]])],"derivedFrom":subQ1}),-1.0]])]});}
            var Q5;
            {var subQ0=sQuery(id+"F3.wireOp",EDGE,"E30");var subQ1=sQuery(id+"F3.wireOp",EDGE,"E11.2");var subQ2=makeQuery(id+"F3.imprint","INTERSECT",VERTEX,{"derivedFrom":[subQ1,subQ0]});Q5=makeQuery(id+"F3.imprint","IMPRINT",FACE,{"disambiguationData":[TD([[makeQuery(id+"F3.imprint","IMPRINT",EDGE,{"disambiguationData":[TD([[subQ2,-1.0]])],"derivedFrom":subQ1}),-1.0]])]});}
            var Q6;
            {var subQ0=sQuery(id+"F3.wireOp",EDGE,"E31");var subQ1=sQuery(id+"F3.wireOp",EDGE,"E11.2");var subQ2=makeQuery(id+"F3.imprint","INTERSECT",VERTEX,{"derivedFrom":[subQ1,subQ0]});Q6=makeQuery(id+"F3.imprint","IMPRINT",FACE,{"disambiguationData":[TD([[makeQuery(id+"F3.imprint","IMPRINT",EDGE,{"disambiguationData":[TD([[subQ2,-1.0]])],"derivedFrom":subQ1}),-1.0]])]});}
            var Q7;
            {var subQ0=sQuery(id+"F3.wireOp",EDGE,"E30");var subQ1=sQuery(id+"F3.wireOp",EDGE,"E11.2");var subQ2=makeQuery(id+"F3.imprint","INTERSECT",VERTEX,{"derivedFrom":[subQ1,subQ0]});Q7=makeQuery(id+"F3.imprint","IMPRINT",FACE,{"disambiguationData":[TD([[makeQuery(id+"F3.imprint","IMPRINT",EDGE,{"disambiguationData":[TD([[subQ2,-1.0]])],"derivedFrom":subQ1}),1.0]])]});}
            var Q8;
            {var subQ0=sQuery(id+"F3.wireOp",EDGE,"E31");var subQ1=sQuery(id+"F3.wireOp",EDGE,"E11.2");var subQ2=makeQuery(id+"F3.imprint","INTERSECT",VERTEX,{"derivedFrom":[subQ1,subQ0]});Q8=makeQuery(id+"F3.imprint","IMPRINT",FACE,{"disambiguationData":[TD([[makeQuery(id+"F3.imprint","IMPRINT",EDGE,{"disambiguationData":[TD([[subQ2,-1.0]])],"derivedFrom":subQ1}),1.0]])]});}
            var Q9;
            {var subQ0=sQuery(id+"F3.wireOp",EDGE,"E34");var subQ1=sQuery(id+"F3.wireOp",EDGE,"E11.2");var subQ2=makeQuery(id+"F3.imprint","INTERSECT",VERTEX,{"derivedFrom":[subQ1,subQ0]});Q9=makeQuery(id+"F3.imprint","IMPRINT",FACE,{"disambiguationData":[TD([[makeQuery(id+"F3.imprint","IMPRINT",EDGE,{"disambiguationData":[TD([[subQ2,-1.0]])],"derivedFrom":subQ1}),1.0]])]});}
            var Q10;
            {var subQ0=sQuery(id+"F3.wireOp",EDGE,"E35");var subQ1=sQuery(id+"F3.wireOp",EDGE,"E11.2");var subQ2=makeQuery(id+"F3.imprint","INTERSECT",VERTEX,{"derivedFrom":[subQ1,subQ0]});Q10=makeQuery(id+"F3.imprint","IMPRINT",FACE,{"disambiguationData":[TD([[makeQuery(id+"F3.imprint","IMPRINT",EDGE,{"disambiguationData":[TD([[subQ2,-1.0]])],"derivedFrom":subQ1}),1.0]])]});}
            var Q11;
            {var subQ0=sQuery(id+"F3.wireOp",EDGE,"E34");var subQ1=sQuery(id+"F3.wireOp",EDGE,"E11.2");var subQ2=makeQuery(id+"F3.imprint","INTERSECT",VERTEX,{"derivedFrom":[subQ1,subQ0]});Q11=makeQuery(id+"F3.imprint","IMPRINT",FACE,{"disambiguationData":[TD([[makeQuery(id+"F3.imprint","IMPRINT",EDGE,{"disambiguationData":[TD([[subQ2,-1.0]])],"derivedFrom":subQ1}),-1.0]])]});}
            var Q12;
            {var subQ0=sQuery(id+"F3.wireOp",EDGE,"E34");var subQ1=sQuery(id+"F3.wireOp",EDGE,"E11.3");var subQ2=makeQuery(id+"F3.imprint","INTERSECT",VERTEX,{"derivedFrom":[subQ1,subQ0]});Q12=makeQuery(id+"F3.imprint","IMPRINT",FACE,{"disambiguationData":[TD([[makeQuery(id+"F3.imprint","IMPRINT",EDGE,{"disambiguationData":[TD([[subQ2,-1.0]])],"derivedFrom":subQ1}),-1.0]])]});}
            var Q13;
            {var subQ0=sQuery(id+"F3.wireOp",EDGE,"E35");var subQ1=sQuery(id+"F3.wireOp",EDGE,"E11.3");var subQ2=makeQuery(id+"F3.imprint","INTERSECT",VERTEX,{"derivedFrom":[subQ1,subQ0]});Q13=makeQuery(id+"F3.imprint","IMPRINT",FACE,{"disambiguationData":[TD([[makeQuery(id+"F3.imprint","IMPRINT",EDGE,{"disambiguationData":[TD([[subQ2,-1.0]])],"derivedFrom":subQ1}),-1.0]])]});}
            var Q14;
            {var subQ0=sQuery(id+"F3.wireOp",EDGE,"E35");var subQ1=sQuery(id+"F3.wireOp",EDGE,"E11.2");var subQ2=makeQuery(id+"F3.imprint","INTERSECT",VERTEX,{"derivedFrom":[subQ1,subQ0]});Q14=makeQuery(id+"F3.imprint","IMPRINT",FACE,{"disambiguationData":[TD([[makeQuery(id+"F3.imprint","IMPRINT",EDGE,{"disambiguationData":[TD([[subQ2,-1.0]])],"derivedFrom":subQ1}),-1.0]])]});}
            extrude(context, id + "F9", {"entities" : qUnion([Q0, Q1, Q2, Q3, Q4, Q5, Q6, Q7, Q8, Q9, Q10, Q11, Q12, Q13, Q14]), "depth" : 4 * mm});
        }
        {
            var Q0;
            {var subQ0=sQuery(id+"F3.wireOp",EDGE,"E14");Q0=makeQuery(id+"F3.imprint","IMPRINT",FACE,{"disambiguationData":[TD([[makeQuery(id+"F3.imprint","IMPRINT",EDGE,{"derivedFrom":subQ0}),-1.0]])]});}
            var Q1;
            {var subQ0=sQuery(id+"F3.wireOp",EDGE,"E23");var subQ1=sQuery(id+"F3.wireOp",EDGE,"E11.2");var subQ2=makeQuery(id+"F3.imprint","INTERSECT",VERTEX,{"derivedFrom":[subQ1,subQ0]});Q1=makeQuery(id+"F3.imprint","IMPRINT",FACE,{"disambiguationData":[TD([[makeQuery(id+"F3.imprint","IMPRINT",EDGE,{"disambiguationData":[TD([[subQ2,-1.0]])],"derivedFrom":subQ1}),-1.0]])]});}
            var Q2;
            {var subQ0=sQuery(id+"F3.wireOp",EDGE,"E11.2");var subQ1=sQuery(id+"F3.wireOp",EDGE,"E10.top");var subQ2=makeQuery(id+"F3.imprint","INTERSECT",VERTEX,{"derivedFrom":[subQ1,subQ0]});Q2=makeQuery(id+"F3.imprint","IMPRINT",FACE,{"disambiguationData":[TD([[makeQuery(id+"F3.imprint","IMPRINT",EDGE,{"disambiguationData":[TD([[subQ2,1.0]])],"derivedFrom":subQ1}),1.0]])]});}
            var Q3;
            {var subQ0=sQuery(id+"F3.wireOp",EDGE,"E30");var subQ1=sQuery(id+"F3.wireOp",EDGE,"E11.2");var subQ2=makeQuery(id+"F3.imprint","INTERSECT",VERTEX,{"derivedFrom":[subQ1,subQ0]});Q3=makeQuery(id+"F3.imprint","IMPRINT",FACE,{"disambiguationData":[TD([[makeQuery(id+"F3.imprint","IMPRINT",EDGE,{"disambiguationData":[TD([[subQ2,-1.0]])],"derivedFrom":subQ1}),-1.0]])]});}
            var Q4;
            {var subQ0=sQuery(id+"F3.wireOp",EDGE,"E31");var subQ1=sQuery(id+"F3.wireOp",EDGE,"E11.2");var subQ2=makeQuery(id+"F3.imprint","INTERSECT",VERTEX,{"derivedFrom":[subQ1,subQ0]});Q4=makeQuery(id+"F3.imprint","IMPRINT",FACE,{"disambiguationData":[TD([[makeQuery(id+"F3.imprint","IMPRINT",EDGE,{"disambiguationData":[TD([[subQ2,-1.0]])],"derivedFrom":subQ1}),-1.0]])]});}
            var Q5;
            {var subQ0=sQuery(id+"F3.wireOp",EDGE,"E20");var subQ1=sQuery(id+"F3.wireOp",EDGE,"E11.2");var subQ2=makeQuery(id+"F3.imprint","INTERSECT",VERTEX,{"derivedFrom":[subQ1,subQ0]});Q5=makeQuery(id+"F3.imprint","IMPRINT",FACE,{"disambiguationData":[TD([[makeQuery(id+"F3.imprint","IMPRINT",EDGE,{"disambiguationData":[TD([[subQ2,-1.0]])],"derivedFrom":subQ1}),-1.0]])]});}
            var Q6;
            {var subQ0=sQuery(id+"F3.wireOp",EDGE,"E33");var subQ1=sQuery(id+"F3.wireOp",EDGE,"E11.2");var subQ2=makeQuery(id+"F3.imprint","INTERSECT",VERTEX,{"derivedFrom":[subQ1,subQ0]});Q6=makeQuery(id+"F3.imprint","IMPRINT",FACE,{"disambiguationData":[TD([[makeQuery(id+"F3.imprint","IMPRINT",EDGE,{"disambiguationData":[TD([[subQ2,-1.0]])],"derivedFrom":subQ1}),-1.0]])]});}
            var Q7;
            {var subQ0=sQuery(id+"F3.wireOp",EDGE,"E35");var subQ1=sQuery(id+"F3.wireOp",EDGE,"E11.2");var subQ2=makeQuery(id+"F3.imprint","INTERSECT",VERTEX,{"derivedFrom":[subQ1,subQ0]});Q7=makeQuery(id+"F3.imprint","IMPRINT",FACE,{"disambiguationData":[TD([[makeQuery(id+"F3.imprint","IMPRINT",EDGE,{"disambiguationData":[TD([[subQ2,-1.0]])],"derivedFrom":subQ1}),-1.0]])]});}
            var Q8;
            {var subQ0=sQuery(id+"F3.wireOp",EDGE,"E34");var subQ1=sQuery(id+"F3.wireOp",EDGE,"E11.2");var subQ2=makeQuery(id+"F3.imprint","INTERSECT",VERTEX,{"derivedFrom":[subQ1,subQ0]});Q8=makeQuery(id+"F3.imprint","IMPRINT",FACE,{"disambiguationData":[TD([[makeQuery(id+"F3.imprint","IMPRINT",EDGE,{"disambiguationData":[TD([[subQ2,-1.0]])],"derivedFrom":subQ1}),-1.0]])]});}
            extrude(context, id + "F10", {"entities" : qUnion([Q0, Q1, Q2, Q3, Q4, Q5, Q6, Q7, Q8]), "operationType" : NewBodyOperationType.ADD, "oppositeDirection" : true, "depth" : 7 * mm});
        }
        {
            var Q0;
            Q0=makeQuery(id+"F2.opExtrude","CAP_FACE",FACE,{"disambiguationData":[OSD([sQuery(id+"F1.wireOp",EDGE,"E8.bottom"),sQuery(id+"F1.wireOp",EDGE,"E8.top"),sQuery(id+"F1.wireOp",EDGE,"E8.left"),sQuery(id+"F1.wireOp",EDGE,"E8.right")])],"isStart":false});
            var sketch = newSketch(context, id + "F11", { "sketchPlane" : qUnion([Q0])});
            skArc(sketch, "E42", {"start": v(-16.47, -13.82) * mm, "mid": v(0, -21.5) * mm, "end": v(16.47, -13.82) * mm});
            skArc(sketch, "E43", {"start": v(-20.3, -17.03) * mm, "mid": v(0, -26.5) * mm, "end": v(20.3, -17.03) * mm});
            skLineSegment(sketch, "E44", {"start": v(-16.47, -13.82) * mm, "end": v(-20.3, -17.03) * mm});
            skLineSegment(sketch, "E45", {"start": v(16.47, -13.82) * mm, "end": v(20.3, -17.03) * mm});
            skSolve(sketch);
        }
        {
            var Q0;
            Q0 = qSketchRegion(id + "F11", true);
            extrude(context, id + "F12", {"entities" : qUnion([Q0]), "oppositeDirection" : true, "depth" : 4 * mm});
        }
        {
            var Q0;
            Q0=makeQuery(id+"F2.opExtrude","SWEPT_FACE",FACE,{"disambiguationData":[OSD([sQuery(id+"F1.wireOp",EDGE,"E8.bottom")])]});
            var sketch = newSketch(context, id + "F13", { "sketchPlane" : qUnion([Q0])});
            skLineSegment(sketch, "E46", {"start": v(-10.5, 15) * mm, "end": v(-30.5, 15) * mm});
            skLineSegment(sketch, "E47", {"start": v(-30.5, 15) * mm, "end": v(-30.5, -25) * mm});
            skLineSegment(sketch, "E48", {"start": v(10.5, 15) * mm, "end": v(30.5, 15) * mm});
            skLineSegment(sketch, "E49", {"start": v(30.5, 15) * mm, "end": v(30.5, -25) * mm});
            skLineSegment(sketch, "E50", {"start": v(-10.5, 15) * mm, "end": v(-10.5, 13) * mm});
            skLineSegment(sketch, "E51", {"start": v(-10.5, 13) * mm, "end": v(-28.5, 13) * mm});
            skLineSegment(sketch, "E52", {"start": v(-28.5, 13) * mm, "end": v(-28.5, -25) * mm});
            skLineSegment(sketch, "E53", {"start": v(-28.5, -25) * mm, "end": v(-30.5, -25) * mm});
            skLineSegment(sketch, "E54", {"start": v(10.5, 15) * mm, "end": v(10.5, 13) * mm});
            skLineSegment(sketch, "E55", {"start": v(10.5, 13) * mm, "end": v(28.5, 13) * mm});
            skLineSegment(sketch, "E56", {"start": v(28.5, 13) * mm, "end": v(28.5, -25) * mm});
            skLineSegment(sketch, "E57", {"start": v(28.5, -25) * mm, "end": v(30.5, -25) * mm});
            skSolve(sketch);
        }
        {
            var Q0;
            Q0=makeQuery(id+"F13.imprint","IMPRINT",FACE,{"disambiguationData":[TD([[makeQuery(id+"F13.imprint","IMPRINT",EDGE,{"derivedFrom":sQuery(id+"F13.wireOp",EDGE,"E46")}),1.0]])]});
            extrude(context, id + "F14", {"entities" : qUnion([Q0]), "oppositeDirection" : true, "depth" : 710 * mm, "offsetDistance" : 25 * mm});
        }
        {
            var Q0;
            Q0=makeQuery(id+"F13.imprint","IMPRINT",FACE,{"disambiguationData":[TD([[makeQuery(id+"F13.imprint","IMPRINT",EDGE,{"derivedFrom":sQuery(id+"F13.wireOp",EDGE,"E48")}),-1.0]])]});
            extrude(context, id + "F15", {"entities" : qUnion([Q0]), "oppositeDirection" : true, "depth" : 710 * mm, "offsetDistance" : 25 * mm});
        }
        {
            var Q0;
            Q0=qCreatedBy(makeId("Right.planeOp"),FACE);
            var sketch = newSketch(context, id + "F16", { "sketchPlane" : qUnion([Q0])});
            skLineSegment(sketch, "E58", {"start": v(105, 0) * mm, "end": v(-45, 0) * mm});
            skLineSegment(sketch, "E59", {"start": v(105, 0) * mm, "end": v(105, 15) * mm});
            skLineSegment(sketch, "E60", {"start": v(-45, 0) * mm, "end": v(-135, -11) * mm});
            skLineSegment(sketch, "E61", {"start": v(-135, -11) * mm, "end": v(-135, -16) * mm});
            skLineSegment(sketch, "E62", {"start": v(-135, -16) * mm, "end": v(-168, -16) * mm});
            skLineSegment(sketch, "E63", {"start": v(-168, -16) * mm, "end": v(-235, -25) * mm});
            skLineSegment(sketch, "E64", {"start": v(-235, -25) * mm, "end": v(105, -25) * mm});
            skLineSegment(sketch, "E65", {"start": v(105, -25) * mm, "end": v(105, 0) * mm});
            skSolve(sketch);
        }
        {
            var Q0;
            Q0 = qSketchRegion(id + "F16", true);
            extrude(context, id + "F17", {"entities" : qUnion([Q0]), "operationType" : NewBodyOperationType.REMOVE, "endBound" : BoundingType.SYMMETRIC, "oppositeDirection" : true, "depth" : 100 * mm});
        }
        {
            var Q0;
            Q0=makeQuery(id+"F2.opExtrude","SWEPT_FACE",FACE,{"disambiguationData":[OSD([sQuery(id+"F1.wireOp",EDGE,"E8.bottom")])]});
            var sketch = newSketch(context, id + "F18", { "sketchPlane" : qUnion([Q0])});
            skLineSegment(sketch, "E66.bottom", {"start": v(-30.5, 15) * mm, "end": v(30.5, 15) * mm});
            skLineSegment(sketch, "E66.top", {"start": v(-30.5, 0) * mm, "end": v(30.5, 0) * mm});
            skLineSegment(sketch, "E66.left", {"start": v(-30.5, 15) * mm, "end": v(-30.5, 0) * mm});
            skLineSegment(sketch, "E66.right", {"start": v(30.5, 15) * mm, "end": v(30.5, 0) * mm});
            skSolve(sketch);
        }
        {
            var Q0;
            Q0=qCreatedBy(makeId("Right.planeOp"),FACE);
            var sketch = newSketch(context, id + "F19", { "sketchPlane" : qUnion([Q0])});
            skLineSegment(sketch, "E67", {"start": v(0, 8.42) * mm, "end": v(0, -12.04) * mm, "construction": true});
            skLineSegment(sketch, "E68", {"start": v(0, 0) * mm, "end": v(-3.5, 0) * mm});
            skLineSegment(sketch, "E69", {"start": v(-3.5, 0) * mm, "end": v(-3.5, -8) * mm});
            skLineSegment(sketch, "E70", {"start": v(-3.5, -8) * mm, "end": v(-5.5, -8) * mm});
            skLineSegment(sketch, "E71", {"start": v(-5.5, -8) * mm, "end": v(-5.5, -11) * mm});
            skLineSegment(sketch, "E72", {"start": v(-5.5, -11) * mm, "end": v(0, -11) * mm});
            skLineSegment(sketch, "E73", {"start": v(0, 0) * mm, "end": v(0, -11) * mm});
            skSolve(sketch);
        }
        {
            var Q0;
            Q0 = qSketchRegion(id + "F18", true);
            extrude(context, id + "F20", {"entities" : qUnion([Q0]), "operationType" : NewBodyOperationType.ADD, "depth" : 16 * mm});
        }
        {
            var Q0;
            Q0=makeQuery(id+"F19.imprint","IMPRINT",FACE,{"disambiguationData":[TD([[makeQuery(id+"F19.imprint","IMPRINT",EDGE,{"derivedFrom":sQuery(id+"F19.wireOp",EDGE,"E68")}),1.0]])]});
            var Q1;
            Q1=sQuery(id+"F19.wireOp",EDGE,"E73");
            revolve(context, id + "F21", {"entities" : qUnion([Q0]), "axis" : qUnion([Q1]), "revolveType" : RevolveType.FULL});
        }
        {
            var Q0;
            Q0=makeQuery(id+"F20.opExtrude","CAP_EDGE",EDGE,{"disambiguationData":[OSD([sQuery(id+"F18.wireOp",EDGE,"E66.top")])],"isStart":false});
            chamfer(context, id + "F22", {"entities" : qUnion([Q0]), "chamferType" : ChamferType.OFFSET_ANGLE, "width" : 12 * mm, "oppositeDirection" : false, "angle" : 50 * degree, "tangentPropagation" : true});
        }
        {
            var Q0;
            {var subQ0=sQuery(id+"F18.wireOp",EDGE,"E66.top");Q0=makeQuery(id+"F22.opChamfer","BLEND_EDGE",EDGE,{"blendedFrom":[makeQuery(id+"F20.opExtrude","CAP_EDGE",EDGE,{"disambiguationData":[OSD([subQ0])],"isStart":false}),makeQuery(id+"F20.opExtrude","CAP_FACE",FACE,{"disambiguationData":[OSD([sQuery(id+"F18.wireOp",EDGE,"E66.bottom"),subQ0,sQuery(id+"F18.wireOp",EDGE,"E66.left"),sQuery(id+"F18.wireOp",EDGE,"E66.right")])],"isStart":false})],"blendedInto":[makeQuery(id+"F20.opExtrude","CAP_FACE",FACE,{"disambiguationData":[OSD([sQuery(id+"F18.wireOp",EDGE,"E66.bottom"),subQ0,sQuery(id+"F18.wireOp",EDGE,"E66.left"),sQuery(id+"F18.wireOp",EDGE,"E66.right")])],"isStart":false})]});}
            var Q1;
            {var subQ0=sQuery(id+"F18.wireOp",EDGE,"E66.top");Q1=makeQuery(id+"F22.opChamfer","BLEND_EDGE",EDGE,{"blendedFrom":[makeQuery(id+"F20.opExtrude","CAP_EDGE",EDGE,{"disambiguationData":[OSD([subQ0])],"isStart":false}),makeQuery(id+"F20.boolean.opBoolean","MERGE",FACE,{"derivedFrom":[makeQuery(id+"F2.opExtrude","CAP_FACE",FACE,{"disambiguationData":[OSD([sQuery(id+"F1.wireOp",EDGE,"E8.bottom"),sQuery(id+"F1.wireOp",EDGE,"E8.top"),sQuery(id+"F1.wireOp",EDGE,"E8.left"),sQuery(id+"F1.wireOp",EDGE,"E8.right")])],"isStart":true}),makeQuery(id+"F20.opExtrude","SWEPT_FACE",FACE,{"disambiguationData":[OSD([subQ0])]})]})],"blendedInto":[makeQuery(id+"F20.boolean.opBoolean","MERGE",FACE,{"derivedFrom":[makeQuery(id+"F2.opExtrude","CAP_FACE",FACE,{"disambiguationData":[OSD([sQuery(id+"F1.wireOp",EDGE,"E8.bottom"),sQuery(id+"F1.wireOp",EDGE,"E8.top"),sQuery(id+"F1.wireOp",EDGE,"E8.left"),sQuery(id+"F1.wireOp",EDGE,"E8.right")])],"isStart":true}),makeQuery(id+"F20.opExtrude","SWEPT_FACE",FACE,{"disambiguationData":[OSD([subQ0])]})]})]});}
            fillet(context, id + "F23", {"entities" : qUnion([Q0, Q1]), "radius" : 3 * mm, "tangentPropagation" : true, "allowEdgeOverflow" : false});
        }
        {
            var Q0;
            Q0=makeQuery(id+"F12.opExtrude","CAP_FACE",FACE,{"disambiguationData":[OSD([sQuery(id+"F11.wireOp",EDGE,"E42"),sQuery(id+"F11.wireOp",EDGE,"E43"),sQuery(id+"F11.wireOp",EDGE,"E44"),sQuery(id+"F11.wireOp",EDGE,"E45")])],"isStart":false});
            var sketch = newSketch(context, id + "F24", { "sketchPlane" : qUnion([Q0])});
            skArc(sketch, "E74", {"start": v(-19.34, 16.23) * mm, "mid": v(0, 25.25) * mm, "end": v(19.34, 16.23) * mm});
            skArc(sketch, "E75", {"start": v(-17.43, 14.62) * mm, "mid": v(0, 22.75) * mm, "end": v(17.43, 14.62) * mm});
            skLineSegment(sketch, "E76", {"start": v(-19.34, 16.23) * mm, "end": v(-17.43, 14.62) * mm});
            skLineSegment(sketch, "E77", {"start": v(17.43, 14.62) * mm, "end": v(19.34, 16.23) * mm});
            skSolve(sketch);
        }
        {
            var Q0;
            Q0 = qSketchRegion(id + "F24", true);
            extrude(context, id + "F25", {"entities" : qUnion([Q0]), "operationType" : NewBodyOperationType.ADD, "depth" : 5 * mm});
        }
        {
            var Q0;
            Q0=sQuery(id+"F3.wireOp",VERTEX,"E36");
            var Q1;
            Q1=sQuery(id+"F3.wireOp",VERTEX,"E37");
            var Q2;
            Q2=makeQuery(id+"F12.opExtrude","SWEPT_BODY",BODY,{"disambiguationData":[OSD([sQuery(id+"F11.wireOp",EDGE,"E42"),sQuery(id+"F11.wireOp",EDGE,"E43"),sQuery(id+"F11.wireOp",EDGE,"E44"),sQuery(id+"F11.wireOp",EDGE,"E45")])]});
            var Q3;
            Q3=makeQuery(id+"F9.opExtrude","SWEPT_BODY",BODY,{"disambiguationData":[OSD([sQuery(id+"F3.wireOp",EDGE,"E20"),sQuery(id+"F3.wireOp",EDGE,"E21"),sQuery(id+"F3.wireOp",EDGE,"E22"),sQuery(id+"F3.wireOp",EDGE,"E23")])]});
            hole(context, id + "F26", {"style" : HoleStyle.SIMPLE, "endStyle" : HoleEndStyle.THROUGH, "oppositeDirection" : true, "holeDiameter" : 1.5 * mm, "tappedDepth" : 12 * mm, "tapClearance" : 3, "locations" : qUnion([Q0, Q1]), "scope" : qUnion([Q2, Q3])});
        }
        {
            var Q0;
            Q0=makeQuery(id+"F9.opExtrude","SWEPT_EDGE",EDGE,{"disambiguationData":[OSD([sQuery(id+"F3.wireOp",EDGE,"E22"),sQuery(id+"F3.wireOp",EDGE,"E23")])]});
            var Q1;
            Q1=makeQuery(id+"F9.opExtrude","SWEPT_EDGE",EDGE,{"disambiguationData":[OSD([sQuery(id+"F3.wireOp",EDGE,"E20"),sQuery(id+"F3.wireOp",EDGE,"E22")])]});
            var Q2;
            Q2=makeQuery(id+"F12.opExtrude","SWEPT_EDGE",EDGE,{"disambiguationData":[OSD([sQuery(id+"F11.wireOp",EDGE,"E42"),sQuery(id+"F11.wireOp",EDGE,"E44")])]});
            var Q3;
            Q3=makeQuery(id+"F12.opExtrude","SWEPT_EDGE",EDGE,{"disambiguationData":[OSD([sQuery(id+"F11.wireOp",EDGE,"E43"),sQuery(id+"F11.wireOp",EDGE,"E44")])]});
            var Q4;
            Q4=makeQuery(id+"F12.opExtrude","SWEPT_EDGE",EDGE,{"disambiguationData":[OSD([sQuery(id+"F11.wireOp",EDGE,"E42"),sQuery(id+"F11.wireOp",EDGE,"E45")])]});
            var Q5;
            Q5=makeQuery(id+"F12.opExtrude","SWEPT_EDGE",EDGE,{"disambiguationData":[OSD([sQuery(id+"F11.wireOp",EDGE,"E43"),sQuery(id+"F11.wireOp",EDGE,"E45")])]});
            var Q6;
            Q6=makeQuery(id+"F9.opExtrude","SWEPT_EDGE",EDGE,{"disambiguationData":[OSD([sQuery(id+"F3.wireOp",EDGE,"E20"),sQuery(id+"F3.wireOp",EDGE,"E21")])]});
            var Q7;
            Q7=makeQuery(id+"F9.opExtrude","SWEPT_EDGE",EDGE,{"disambiguationData":[OSD([sQuery(id+"F3.wireOp",EDGE,"E21"),sQuery(id+"F3.wireOp",EDGE,"E23")])]});
            var Q8;
            Q8=makeQuery(id+"F25.opExtrude","SWEPT_EDGE",EDGE,{"disambiguationData":[OSD([sQuery(id+"F11.wireOp",EDGE,"E45"),sQuery(id+"F24.wireOp",EDGE,"E75"),sQuery(id+"F24.wireOp",EDGE,"E77")])]});
            var Q9;
            Q9=makeQuery(id+"F25.opExtrude","SWEPT_EDGE",EDGE,{"disambiguationData":[OSD([sQuery(id+"F11.wireOp",EDGE,"E45"),sQuery(id+"F24.wireOp",EDGE,"E74"),sQuery(id+"F24.wireOp",EDGE,"E77")])]});
            var Q10;
            Q10=makeQuery(id+"F25.opExtrude","SWEPT_EDGE",EDGE,{"disambiguationData":[OSD([sQuery(id+"F11.wireOp",EDGE,"E44"),sQuery(id+"F24.wireOp",EDGE,"E75"),sQuery(id+"F24.wireOp",EDGE,"E76")])]});
            var Q11;
            Q11=makeQuery(id+"F25.opExtrude","SWEPT_EDGE",EDGE,{"disambiguationData":[OSD([sQuery(id+"F11.wireOp",EDGE,"E44"),sQuery(id+"F24.wireOp",EDGE,"E74"),sQuery(id+"F24.wireOp",EDGE,"E76")])]});
            var Q12;
            Q12=makeQuery(id+"F10.opExtrude","CAP_EDGE",EDGE,{"disambiguationData":[OSD([sQuery(id+"F3.wireOp",EDGE,"E11.3")])],"isStart":false});
            var Q13;
            Q13=makeQuery(id+"F10.opExtrude","CAP_EDGE",EDGE,{"disambiguationData":[OSD([sQuery(id+"F3.wireOp",EDGE,"E11.2")])],"isStart":false});
            var Q14;
            Q14=makeQuery(id+"F10.opExtrude","CAP_EDGE",EDGE,{"disambiguationData":[OSD([sQuery(id+"F3.wireOp",EDGE,"E14")])],"isStart":false});
            var Q15;
            Q15=makeQuery(id+"F10.opExtrude","CAP_EDGE",EDGE,{"disambiguationData":[OSD([sQuery(id+"F3.wireOp",EDGE,"E14")])],"isStart":true});
            var Q16;
            Q16=makeQuery(id+"F10.opExtrude","SWEPT_EDGE",EDGE,{"disambiguationData":[OSD([sQuery(id+"F3.wireOp",EDGE,"E10.top"),sQuery(id+"F3.wireOp",EDGE,"E11.2")])]});
            var Q17;
            Q17=makeQuery(id+"F10.opExtrude","CAP_EDGE",EDGE,{"disambiguationData":[OSD([sQuery(id+"F3.wireOp",EDGE,"E10.top")])],"isStart":false});
            var Q18;
            Q18=makeQuery(id+"F10.opExtrude","SWEPT_EDGE",EDGE,{"disambiguationData":[OSD([sQuery(id+"F3.wireOp",EDGE,"E10.top"),sQuery(id+"F3.wireOp",EDGE,"E11.3")])]});
            var Q19;
            Q19=makeQuery(id+"F10.opExtrude","SWEPT_EDGE",EDGE,{"disambiguationData":[OSD([sQuery(id+"F3.wireOp",EDGE,"E11.3"),sQuery(id+"F3.wireOp",EDGE,"E14")])]});
            var Q20;
            Q20=makeQuery(id+"F10.opExtrude","SWEPT_EDGE",EDGE,{"disambiguationData":[OSD([sQuery(id+"F3.wireOp",EDGE,"E11.2"),sQuery(id+"F3.wireOp",EDGE,"E14")])]});
            var Q21;
            Q21=makeQuery(id+"F10.opExtrude","CAP_EDGE",EDGE,{"disambiguationData":[OSD([sQuery(id+"F3.wireOp",EDGE,"E10.top")])],"isStart":true});
            chamfer(context, id + "F27", {"entities" : qUnion([Q0, Q1, Q2, Q3, Q4, Q5, Q6, Q7, Q8, Q9, Q10, Q11, Q12, Q13, Q14, Q15, Q16, Q17, Q18, Q19, Q20, Q21]), "width" : 1 * mm, "tangentPropagation" : true});
        }
        {
            var Q0;
            Q0=makeQuery(id+"F9.opExtrude","CAP_EDGE",EDGE,{"disambiguationData":[OSD([sQuery(id+"F3.wireOp",EDGE,"E23")])],"isStart":false});
            var Q1;
            {var subQ0=sQuery(id+"F3.wireOp",EDGE,"E23");var subQ1=sQuery(id+"F3.wireOp",EDGE,"E22");Q1=makeQuery(id+"F27.opChamfer","BLEND_EDGE",EDGE,{"blendedFrom":[makeQuery(id+"F9.opExtrude","SWEPT_EDGE",EDGE,{"disambiguationData":[OSD([subQ1,subQ0])]}),makeQuery(id+"F9.opExtrude","CAP_FACE",FACE,{"disambiguationData":[OSD([sQuery(id+"F3.wireOp",EDGE,"E20"),sQuery(id+"F3.wireOp",EDGE,"E21"),subQ1,subQ0])],"isStart":false})],"blendedInto":[makeQuery(id+"F9.opExtrude","CAP_FACE",FACE,{"disambiguationData":[OSD([sQuery(id+"F3.wireOp",EDGE,"E20"),sQuery(id+"F3.wireOp",EDGE,"E21"),subQ1,subQ0])],"isStart":false})]});}
            var Q2;
            Q2=makeQuery(id+"F9.opExtrude","CAP_EDGE",EDGE,{"disambiguationData":[OSD([sQuery(id+"F3.wireOp",EDGE,"E22")])],"isStart":false});
            var Q3;
            {var subQ0=sQuery(id+"F3.wireOp",EDGE,"E23");var subQ1=sQuery(id+"F3.wireOp",EDGE,"E21");Q3=makeQuery(id+"F27.opChamfer","BLEND_EDGE",EDGE,{"blendedFrom":[makeQuery(id+"F9.opExtrude","SWEPT_EDGE",EDGE,{"disambiguationData":[OSD([subQ1,subQ0])]}),makeQuery(id+"F9.opExtrude","CAP_FACE",FACE,{"disambiguationData":[OSD([sQuery(id+"F3.wireOp",EDGE,"E20"),subQ1,sQuery(id+"F3.wireOp",EDGE,"E22"),subQ0])],"isStart":false})],"blendedInto":[makeQuery(id+"F9.opExtrude","CAP_FACE",FACE,{"disambiguationData":[OSD([sQuery(id+"F3.wireOp",EDGE,"E20"),subQ1,sQuery(id+"F3.wireOp",EDGE,"E22"),subQ0])],"isStart":false})]});}
            var Q4;
            Q4=makeQuery(id+"F9.opExtrude","CAP_EDGE",EDGE,{"disambiguationData":[OSD([sQuery(id+"F3.wireOp",EDGE,"E21")])],"isStart":false});
            var Q5;
            {var subQ0=sQuery(id+"F3.wireOp",EDGE,"E21");var subQ1=sQuery(id+"F3.wireOp",EDGE,"E20");Q5=makeQuery(id+"F27.opChamfer","BLEND_EDGE",EDGE,{"blendedFrom":[makeQuery(id+"F9.opExtrude","SWEPT_EDGE",EDGE,{"disambiguationData":[OSD([subQ1,subQ0])]}),makeQuery(id+"F9.opExtrude","CAP_FACE",FACE,{"disambiguationData":[OSD([subQ1,subQ0,sQuery(id+"F3.wireOp",EDGE,"E22"),sQuery(id+"F3.wireOp",EDGE,"E23")])],"isStart":false})],"blendedInto":[makeQuery(id+"F9.opExtrude","CAP_FACE",FACE,{"disambiguationData":[OSD([subQ1,subQ0,sQuery(id+"F3.wireOp",EDGE,"E22"),sQuery(id+"F3.wireOp",EDGE,"E23")])],"isStart":false})]});}
            var Q6;
            Q6=makeQuery(id+"F9.opExtrude","CAP_EDGE",EDGE,{"disambiguationData":[OSD([sQuery(id+"F3.wireOp",EDGE,"E20")])],"isStart":false});
            var Q7;
            {var subQ0=sQuery(id+"F3.wireOp",EDGE,"E11.2");var subQ1=sQuery(id+"F3.wireOp",EDGE,"E10.top");var subQ2=makeQuery(id+"F10.opExtrude","CAP_FACE",FACE,{"disambiguationData":[OSD([subQ1,subQ0,sQuery(id+"F3.wireOp",EDGE,"E11.3"),sQuery(id+"F3.wireOp",EDGE,"E14")])],"isStart":true});var subQ3=sQuery(id+"F3.wireOp",EDGE,"E20");var subQ4=makeQuery(id+"F10.opExtrude","SWEPT_FACE",FACE,{"disambiguationData":[OSD([subQ0])]});Q7=makeQuery(id+"F10.boolean.opBoolean","SPLIT",EDGE,{"disambiguationData":[topologyDisambiguationEdgeConnected([subQ2,subQ4]),TD([makeQuery(id+"F9.opExtrude","SWEPT_FACE",FACE,{"disambiguationData":[OSD([subQ3])]})])],"derivedFrom":makeQuery(id+"F10.opExtrude","CAP_EDGE",EDGE,{"disambiguationData":[OSD([subQ0])],"isStart":true})});}
            var Q8;
            {var subQ0=sQuery(id+"F3.wireOp",EDGE,"E11.2");var subQ1=makeQuery(id+"F10.opExtrude","SWEPT_FACE",FACE,{"disambiguationData":[OSD([subQ0])]});var subQ2=sQuery(id+"F3.wireOp",EDGE,"E14");var subQ3=makeQuery(id+"F10.opExtrude","CAP_FACE",FACE,{"disambiguationData":[OSD([sQuery(id+"F3.wireOp",EDGE,"E10.top"),subQ0,sQuery(id+"F3.wireOp",EDGE,"E11.3"),subQ2])],"isStart":true});var subQ4=sQuery(id+"F3.wireOp",EDGE,"E23");Q8=makeQuery(id+"F10.boolean.opBoolean","SPLIT",EDGE,{"disambiguationData":[topologyDisambiguationEdgeConnected([subQ3,subQ1]),TD([makeQuery(id+"F9.opExtrude","SWEPT_FACE",FACE,{"disambiguationData":[OSD([subQ4])]})])],"derivedFrom":makeQuery(id+"F10.opExtrude","CAP_EDGE",EDGE,{"disambiguationData":[OSD([subQ0])],"isStart":true})});}
            var Q9;
            {var subQ0=sQuery(id+"F3.wireOp",EDGE,"E14");var subQ1=sQuery(id+"F3.wireOp",EDGE,"E11.3");var subQ2=makeQuery(id+"F10.opExtrude","CAP_FACE",FACE,{"disambiguationData":[OSD([sQuery(id+"F3.wireOp",EDGE,"E10.top"),sQuery(id+"F3.wireOp",EDGE,"E11.2"),subQ1,subQ0])],"isStart":true});var subQ3=sQuery(id+"F3.wireOp",EDGE,"E23");var subQ4=makeQuery(id+"F10.opExtrude","SWEPT_FACE",FACE,{"disambiguationData":[OSD([subQ1])]});Q9=makeQuery(id+"F10.boolean.opBoolean","SPLIT",EDGE,{"disambiguationData":[topologyDisambiguationEdgeConnected([subQ2,subQ4]),TD([makeQuery(id+"F9.opExtrude","SWEPT_FACE",FACE,{"disambiguationData":[OSD([subQ3])]})])],"derivedFrom":makeQuery(id+"F10.opExtrude","CAP_EDGE",EDGE,{"disambiguationData":[OSD([subQ1])],"isStart":true})});}
            var Q10;
            {var subQ0=sQuery(id+"F3.wireOp",EDGE,"E11.3");var subQ1=sQuery(id+"F3.wireOp",EDGE,"E10.top");var subQ2=makeQuery(id+"F10.opExtrude","CAP_FACE",FACE,{"disambiguationData":[OSD([subQ1,sQuery(id+"F3.wireOp",EDGE,"E11.2"),subQ0,sQuery(id+"F3.wireOp",EDGE,"E14")])],"isStart":true});var subQ3=sQuery(id+"F3.wireOp",EDGE,"E20");var subQ4=makeQuery(id+"F10.opExtrude","SWEPT_FACE",FACE,{"disambiguationData":[OSD([subQ0])]});Q10=makeQuery(id+"F10.boolean.opBoolean","SPLIT",EDGE,{"disambiguationData":[topologyDisambiguationEdgeConnected([subQ2,subQ4]),TD([makeQuery(id+"F9.opExtrude","SWEPT_FACE",FACE,{"disambiguationData":[OSD([subQ3])]})])],"derivedFrom":makeQuery(id+"F10.opExtrude","CAP_EDGE",EDGE,{"disambiguationData":[OSD([subQ0])],"isStart":true})});}
            var Q11;
            {var subQ0=sQuery(id+"F3.wireOp",EDGE,"E22");var subQ1=sQuery(id+"F3.wireOp",EDGE,"E20");Q11=makeQuery(id+"F27.opChamfer","BLEND_EDGE",EDGE,{"blendedFrom":[makeQuery(id+"F9.opExtrude","SWEPT_EDGE",EDGE,{"disambiguationData":[OSD([subQ1,subQ0])]}),makeQuery(id+"F9.opExtrude","CAP_FACE",FACE,{"disambiguationData":[OSD([subQ1,sQuery(id+"F3.wireOp",EDGE,"E21"),subQ0,sQuery(id+"F3.wireOp",EDGE,"E23")])],"isStart":false})],"blendedInto":[makeQuery(id+"F9.opExtrude","CAP_FACE",FACE,{"disambiguationData":[OSD([subQ1,sQuery(id+"F3.wireOp",EDGE,"E21"),subQ0,sQuery(id+"F3.wireOp",EDGE,"E23")])],"isStart":false})]});}
            var Q12;
            Q12=makeQuery(id+"F25.opExtrude","CAP_EDGE",EDGE,{"disambiguationData":[OSD([sQuery(id+"F24.wireOp",EDGE,"E75")])],"isStart":false});
            var Q13;
            {var subQ0=sQuery(id+"F24.wireOp",EDGE,"E77");var subQ1=sQuery(id+"F24.wireOp",EDGE,"E75");Q13=makeQuery(id+"F27.opChamfer","BLEND_EDGE",EDGE,{"blendedFrom":[makeQuery(id+"F25.opExtrude","SWEPT_EDGE",EDGE,{"disambiguationData":[OSD([sQuery(id+"F11.wireOp",EDGE,"E45"),subQ1,subQ0])]}),makeQuery(id+"F25.opExtrude","CAP_FACE",FACE,{"disambiguationData":[OSD([sQuery(id+"F24.wireOp",EDGE,"E74"),subQ1,sQuery(id+"F24.wireOp",EDGE,"E76"),subQ0])],"isStart":false})],"blendedInto":[makeQuery(id+"F25.opExtrude","CAP_FACE",FACE,{"disambiguationData":[OSD([sQuery(id+"F24.wireOp",EDGE,"E74"),subQ1,sQuery(id+"F24.wireOp",EDGE,"E76"),subQ0])],"isStart":false})]});}
            var Q14;
            {var subQ0=sQuery(id+"F24.wireOp",EDGE,"E77");var subQ1=sQuery(id+"F24.wireOp",EDGE,"E74");Q14=makeQuery(id+"F27.opChamfer","BLEND_EDGE",EDGE,{"blendedFrom":[makeQuery(id+"F25.opExtrude","SWEPT_EDGE",EDGE,{"disambiguationData":[OSD([sQuery(id+"F11.wireOp",EDGE,"E45"),subQ1,subQ0])]}),makeQuery(id+"F25.opExtrude","CAP_FACE",FACE,{"disambiguationData":[OSD([subQ1,sQuery(id+"F24.wireOp",EDGE,"E75"),sQuery(id+"F24.wireOp",EDGE,"E76"),subQ0])],"isStart":false})],"blendedInto":[makeQuery(id+"F25.opExtrude","CAP_FACE",FACE,{"disambiguationData":[OSD([subQ1,sQuery(id+"F24.wireOp",EDGE,"E75"),sQuery(id+"F24.wireOp",EDGE,"E76"),subQ0])],"isStart":false})]});}
            var Q15;
            Q15=makeQuery(id+"F25.opExtrude","CAP_EDGE",EDGE,{"disambiguationData":[OSD([sQuery(id+"F24.wireOp",EDGE,"E74")])],"isStart":false});
            var Q16;
            {var subQ0=sQuery(id+"F24.wireOp",EDGE,"E76");var subQ1=sQuery(id+"F24.wireOp",EDGE,"E74");Q16=makeQuery(id+"F27.opChamfer","BLEND_EDGE",EDGE,{"blendedFrom":[makeQuery(id+"F25.opExtrude","SWEPT_EDGE",EDGE,{"disambiguationData":[OSD([sQuery(id+"F11.wireOp",EDGE,"E44"),subQ1,subQ0])]}),makeQuery(id+"F25.opExtrude","CAP_FACE",FACE,{"disambiguationData":[OSD([subQ1,sQuery(id+"F24.wireOp",EDGE,"E75"),subQ0,sQuery(id+"F24.wireOp",EDGE,"E77")])],"isStart":false})],"blendedInto":[makeQuery(id+"F25.opExtrude","CAP_FACE",FACE,{"disambiguationData":[OSD([subQ1,sQuery(id+"F24.wireOp",EDGE,"E75"),subQ0,sQuery(id+"F24.wireOp",EDGE,"E77")])],"isStart":false})]});}
            var Q17;
            {var subQ0=sQuery(id+"F24.wireOp",EDGE,"E76");var subQ1=sQuery(id+"F24.wireOp",EDGE,"E75");Q17=makeQuery(id+"F27.opChamfer","BLEND_EDGE",EDGE,{"blendedFrom":[makeQuery(id+"F25.opExtrude","SWEPT_EDGE",EDGE,{"disambiguationData":[OSD([sQuery(id+"F11.wireOp",EDGE,"E44"),subQ1,subQ0])]}),makeQuery(id+"F25.opExtrude","CAP_FACE",FACE,{"disambiguationData":[OSD([sQuery(id+"F24.wireOp",EDGE,"E74"),subQ1,subQ0,sQuery(id+"F24.wireOp",EDGE,"E77")])],"isStart":false})],"blendedInto":[makeQuery(id+"F25.opExtrude","CAP_FACE",FACE,{"disambiguationData":[OSD([sQuery(id+"F24.wireOp",EDGE,"E74"),subQ1,subQ0,sQuery(id+"F24.wireOp",EDGE,"E77")])],"isStart":false})]});}
            var Q18;
            Q18=makeQuery(id+"F12.opExtrude","CAP_EDGE",EDGE,{"disambiguationData":[OSD([sQuery(id+"F11.wireOp",EDGE,"E43")])],"isStart":false});
            var Q19;
            {var subQ0=sQuery(id+"F11.wireOp",EDGE,"E45");var subQ1=sQuery(id+"F11.wireOp",EDGE,"E44");var subQ2=sQuery(id+"F11.wireOp",EDGE,"E43");Q19=makeQuery(id+"F27.opChamfer","BLEND_EDGE",EDGE,{"blendedFrom":[makeQuery(id+"F12.opExtrude","SWEPT_EDGE",EDGE,{"disambiguationData":[OSD([subQ2,subQ1])]}),makeQuery(id+"F25.boolean.opBoolean","SPLIT",FACE,{"disambiguationData":[TD([makeQuery(id+"F12.opExtrude","SWEPT_FACE",FACE,{"disambiguationData":[OSD([subQ2])]})])],"derivedFrom":makeQuery(id+"F12.opExtrude","CAP_FACE",FACE,{"disambiguationData":[OSD([sQuery(id+"F11.wireOp",EDGE,"E42"),subQ2,subQ1,subQ0])],"isStart":false})})],"blendedInto":[makeQuery(id+"F25.boolean.opBoolean","SPLIT",FACE,{"disambiguationData":[TD([makeQuery(id+"F12.opExtrude","SWEPT_FACE",FACE,{"disambiguationData":[OSD([subQ2])]})])],"derivedFrom":makeQuery(id+"F12.opExtrude","CAP_FACE",FACE,{"disambiguationData":[OSD([sQuery(id+"F11.wireOp",EDGE,"E42"),subQ2,subQ1,subQ0])],"isStart":false})})]});}
            var Q20;
            {var subQ0=sQuery(id+"F11.wireOp",EDGE,"E44");var subQ1=sQuery(id+"F11.wireOp",EDGE,"E43");Q20=makeQuery(id+"F25.boolean.opBoolean","SPLIT",EDGE,{"disambiguationData":[TD([makeQuery(id+"F12.opExtrude","SWEPT_FACE",FACE,{"disambiguationData":[OSD([subQ1])]})])],"derivedFrom":makeQuery(id+"F12.opExtrude","CAP_EDGE",EDGE,{"disambiguationData":[OSD([subQ0])],"isStart":false})});}
            var Q21;
            {var subQ0=sQuery(id+"F11.wireOp",EDGE,"E44");var subQ1=sQuery(id+"F11.wireOp",EDGE,"E42");Q21=makeQuery(id+"F25.boolean.opBoolean","SPLIT",EDGE,{"disambiguationData":[TD([makeQuery(id+"F12.opExtrude","SWEPT_FACE",FACE,{"disambiguationData":[OSD([subQ1])]})])],"derivedFrom":makeQuery(id+"F12.opExtrude","CAP_EDGE",EDGE,{"disambiguationData":[OSD([subQ0])],"isStart":false})});}
            var Q22;
            Q22=makeQuery(id+"F12.opExtrude","CAP_EDGE",EDGE,{"disambiguationData":[OSD([sQuery(id+"F11.wireOp",EDGE,"E42")])],"isStart":false});
            var Q23;
            {var subQ0=sQuery(id+"F11.wireOp",EDGE,"E44");var subQ1=sQuery(id+"F11.wireOp",EDGE,"E45");var subQ2=sQuery(id+"F11.wireOp",EDGE,"E42");Q23=makeQuery(id+"F27.opChamfer","BLEND_EDGE",EDGE,{"blendedFrom":[makeQuery(id+"F12.opExtrude","SWEPT_EDGE",EDGE,{"disambiguationData":[OSD([subQ2,subQ0])]}),makeQuery(id+"F25.boolean.opBoolean","SPLIT",FACE,{"disambiguationData":[TD([makeQuery(id+"F12.opExtrude","SWEPT_FACE",FACE,{"disambiguationData":[OSD([subQ2])]})])],"derivedFrom":makeQuery(id+"F12.opExtrude","CAP_FACE",FACE,{"disambiguationData":[OSD([subQ2,sQuery(id+"F11.wireOp",EDGE,"E43"),subQ0,subQ1])],"isStart":false})})],"blendedInto":[makeQuery(id+"F25.boolean.opBoolean","SPLIT",FACE,{"disambiguationData":[TD([makeQuery(id+"F12.opExtrude","SWEPT_FACE",FACE,{"disambiguationData":[OSD([subQ2])]})])],"derivedFrom":makeQuery(id+"F12.opExtrude","CAP_FACE",FACE,{"disambiguationData":[OSD([subQ2,sQuery(id+"F11.wireOp",EDGE,"E43"),subQ0,subQ1])],"isStart":false})})]});}
            var Q24;
            {var subQ0=sQuery(id+"F11.wireOp",EDGE,"E44");var subQ1=sQuery(id+"F11.wireOp",EDGE,"E45");var subQ2=sQuery(id+"F11.wireOp",EDGE,"E42");Q24=makeQuery(id+"F27.opChamfer","BLEND_EDGE",EDGE,{"blendedFrom":[makeQuery(id+"F12.opExtrude","SWEPT_EDGE",EDGE,{"disambiguationData":[OSD([subQ2,subQ1])]}),makeQuery(id+"F25.boolean.opBoolean","SPLIT",FACE,{"disambiguationData":[TD([makeQuery(id+"F12.opExtrude","SWEPT_FACE",FACE,{"disambiguationData":[OSD([subQ2])]})])],"derivedFrom":makeQuery(id+"F12.opExtrude","CAP_FACE",FACE,{"disambiguationData":[OSD([subQ2,sQuery(id+"F11.wireOp",EDGE,"E43"),subQ0,subQ1])],"isStart":false})})],"blendedInto":[makeQuery(id+"F25.boolean.opBoolean","SPLIT",FACE,{"disambiguationData":[TD([makeQuery(id+"F12.opExtrude","SWEPT_FACE",FACE,{"disambiguationData":[OSD([subQ2])]})])],"derivedFrom":makeQuery(id+"F12.opExtrude","CAP_FACE",FACE,{"disambiguationData":[OSD([subQ2,sQuery(id+"F11.wireOp",EDGE,"E43"),subQ0,subQ1])],"isStart":false})})]});}
            var Q25;
            {var subQ0=sQuery(id+"F11.wireOp",EDGE,"E45");var subQ1=sQuery(id+"F11.wireOp",EDGE,"E42");Q25=makeQuery(id+"F25.boolean.opBoolean","SPLIT",EDGE,{"disambiguationData":[TD([makeQuery(id+"F12.opExtrude","SWEPT_FACE",FACE,{"disambiguationData":[OSD([subQ1])]})])],"derivedFrom":makeQuery(id+"F12.opExtrude","CAP_EDGE",EDGE,{"disambiguationData":[OSD([subQ0])],"isStart":false})});}
            var Q26;
            {var subQ0=sQuery(id+"F11.wireOp",EDGE,"E45");var subQ1=sQuery(id+"F11.wireOp",EDGE,"E43");Q26=makeQuery(id+"F25.boolean.opBoolean","SPLIT",EDGE,{"disambiguationData":[TD([makeQuery(id+"F12.opExtrude","SWEPT_FACE",FACE,{"disambiguationData":[OSD([subQ1])]})])],"derivedFrom":makeQuery(id+"F12.opExtrude","CAP_EDGE",EDGE,{"disambiguationData":[OSD([subQ0])],"isStart":false})});}
            var Q27;
            {var subQ0=sQuery(id+"F11.wireOp",EDGE,"E45");var subQ1=sQuery(id+"F11.wireOp",EDGE,"E44");var subQ2=sQuery(id+"F11.wireOp",EDGE,"E43");Q27=makeQuery(id+"F27.opChamfer","BLEND_EDGE",EDGE,{"blendedFrom":[makeQuery(id+"F12.opExtrude","SWEPT_EDGE",EDGE,{"disambiguationData":[OSD([subQ2,subQ0])]}),makeQuery(id+"F25.boolean.opBoolean","SPLIT",FACE,{"disambiguationData":[TD([makeQuery(id+"F12.opExtrude","SWEPT_FACE",FACE,{"disambiguationData":[OSD([subQ2])]})])],"derivedFrom":makeQuery(id+"F12.opExtrude","CAP_FACE",FACE,{"disambiguationData":[OSD([sQuery(id+"F11.wireOp",EDGE,"E42"),subQ2,subQ1,subQ0])],"isStart":false})})],"blendedInto":[makeQuery(id+"F25.boolean.opBoolean","SPLIT",FACE,{"disambiguationData":[TD([makeQuery(id+"F12.opExtrude","SWEPT_FACE",FACE,{"disambiguationData":[OSD([subQ2])]})])],"derivedFrom":makeQuery(id+"F12.opExtrude","CAP_FACE",FACE,{"disambiguationData":[OSD([sQuery(id+"F11.wireOp",EDGE,"E42"),subQ2,subQ1,subQ0])],"isStart":false})})]});}
            fillet(context, id + "F28", {"entities" : qUnion([Q0, Q1, Q2, Q3, Q4, Q5, Q6, Q7, Q8, Q9, Q10, Q11, Q12, Q13, Q14, Q15, Q16, Q17, Q18, Q19, Q20, Q21, Q22, Q23, Q24, Q25, Q26, Q27]), "radius" : 0.5 * mm, "tangentPropagation" : true, "allowEdgeOverflow" : false});
        }
    });
